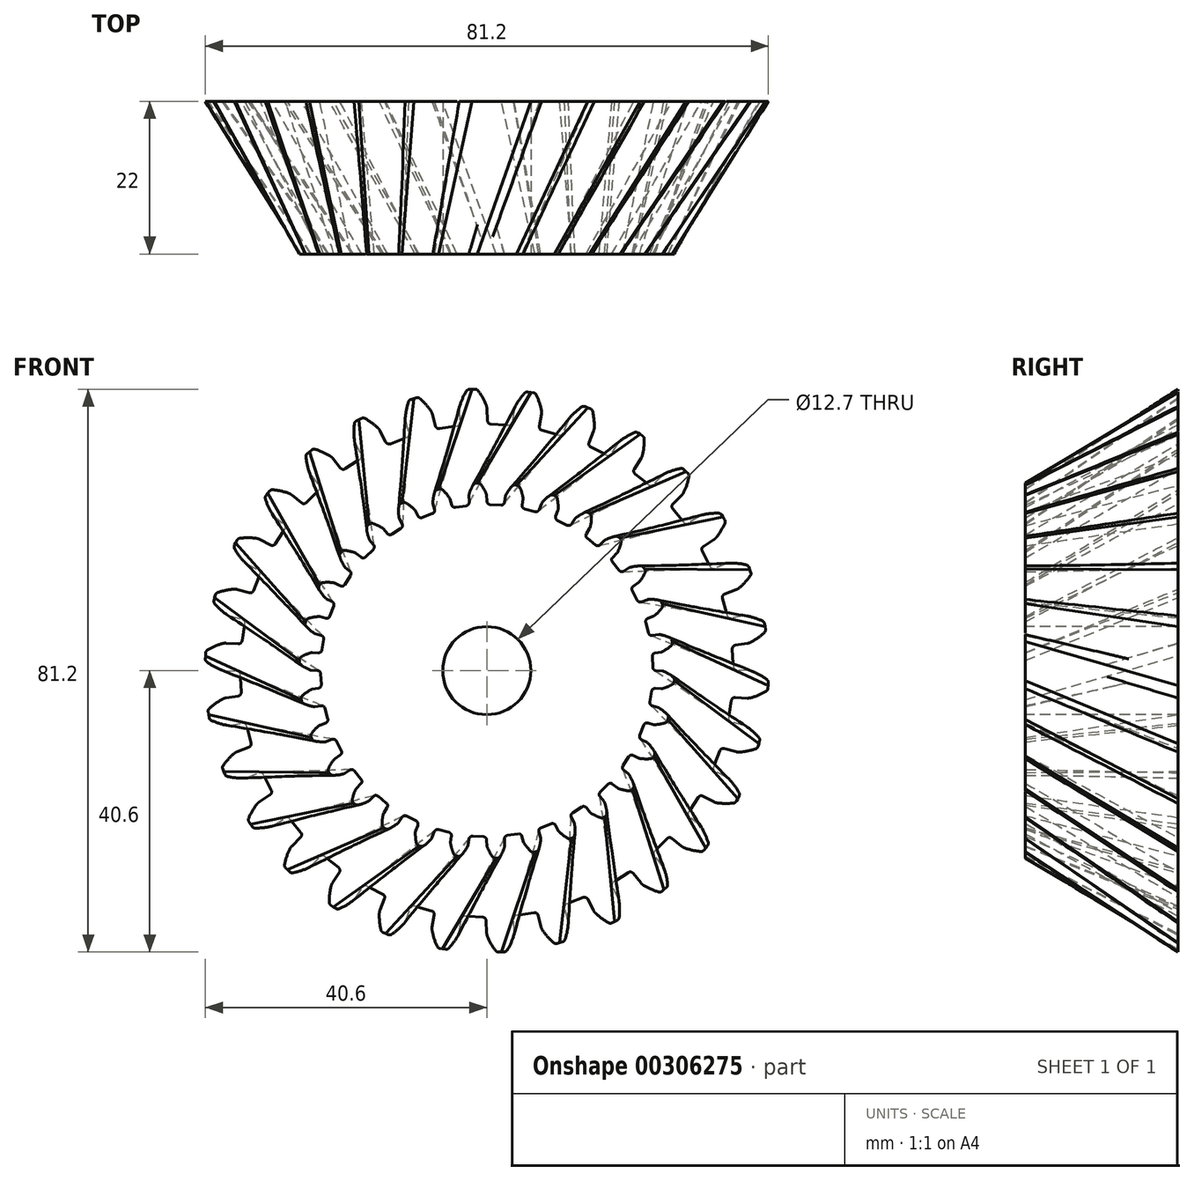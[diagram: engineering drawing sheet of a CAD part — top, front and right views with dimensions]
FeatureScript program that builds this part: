
annotation { "Feature Type Name" : "Feature", "Feature Type Description" : "" }
export const myFeature = defineFeature(function(context is Context, id is Id, definition is map)
    precondition{}
    {
        {
            var Q0;
            Q0=qCreatedBy(makeId("Front.planeOp"),FACE);
            var sketch = newSketch(context, id + "F0", { "sketchPlane" : qUnion([Q0])});
            skArc(sketch, "E0", {"start": v(-0.07, 25.48) * mm, "mid": v(-0.4, 26.19) * mm, "end": v(-0.83, 26.85) * mm});
            skLineSegment(sketch, "E1", {"start": v(-1.24, 27.06) * mm, "end": v(-1.82, 27.06) * mm});
            skLineSegment(sketch, "E2", {"start": v(-0.04, 25.32) * mm, "end": v(0, 24.44) * mm});
            skArc(sketch, "E3.MirrorCS", {"start": v(-2.56, 25.38) * mm, "mid": v(-2.3, 26.1) * mm, "end": v(-1.97, 26.78) * mm});
            skLineSegment(sketch, "E4.MirrorCS", {"start": v(-1.58, 27.03) * mm, "end": v(-0.9, 27.1) * mm});
            skLineSegment(sketch, "E5.MirrorCS", {"start": v(-2.58, 25.21) * mm, "end": v(-2.54, 24.3) * mm});
            skPoint(sketch, "E6.visualSharp", {"position": v(-2.5, 23.57) * mm});
            skArc(sketch, "E6.filletArc", {"start": v(-2.97, 23.78) * mm, "mid": v(-2.65, 23.96) * mm, "end": v(-2.54, 24.3) * mm});
            skPoint(sketch, "E7.visualSharp", {"position": v(0.05, 23.7) * mm});
            skArc(sketch, "E7.filletArc", {"start": v(0, 24.44) * mm, "mid": v(0.16, 24.1) * mm, "end": v(0.5, 23.96) * mm});
            skPoint(sketch, "E8.visualSharp", {"position": v(-2.59, 25.3) * mm});
            skArc(sketch, "E8.filletArc", {"start": v(-2.56, 25.38) * mm, "mid": v(-2.58, 25.3) * mm, "end": v(-2.58, 25.21) * mm});
            skPoint(sketch, "E9.visualSharp", {"position": v(-0.04, 25.4) * mm});
            skArc(sketch, "E9.filletArc", {"start": v(-0.04, 25.32) * mm, "mid": v(-0.05, 25.4) * mm, "end": v(-0.07, 25.48) * mm});
            skPoint(sketch, "E10.visualSharp", {"position": v(-0.99, 27.06) * mm});
            skArc(sketch, "E10.filletArc", {"start": v(-0.83, 26.85) * mm, "mid": v(-1, 27) * mm, "end": v(-1.24, 27.06) * mm});
            skPoint(sketch, "E11.visualSharp", {"position": v(-1.83, 27) * mm});
            skArc(sketch, "E11.filletArc", {"start": v(-1.58, 27.03) * mm, "mid": v(-1.8, 26.95) * mm, "end": v(-1.97, 26.78) * mm});
            skPoint(sketch, "E12.1.0", {"position": v(-6.6, 26.26) * mm});
            skLineSegment(sketch, "E12.1.1", {"start": v(-5.3, 24.75) * mm, "end": v(-5.07, 23.9) * mm});
            skArc(sketch, "E12.1.2", {"start": v(-5.07, 23.9) * mm, "mid": v(-4.85, 23.6) * mm, "end": v(-4.5, 23.54) * mm});
            skPoint(sketch, "E12.1.3", {"position": v(-4.88, 23.2) * mm});
            skArc(sketch, "E12.1.4", {"start": v(-7.78, 24.29) * mm, "mid": v(-7.69, 25.05) * mm, "end": v(-7.5, 25.78) * mm});
            skArc(sketch, "E12.1.5", {"start": v(-7.85, 22.64) * mm, "mid": v(-7.57, 22.88) * mm, "end": v(-7.53, 23.25) * mm});
            skLineSegment(sketch, "E12.1.6", {"start": v(-7.77, 24.12) * mm, "end": v(-7.53, 23.25) * mm});
            skArc(sketch, "E12.1.7", {"start": v(-5.37, 24.9) * mm, "mid": v(-5.84, 25.53) * mm, "end": v(-6.4, 26.09) * mm});
            skPoint(sketch, "E12.1.8", {"position": v(-7.34, 22.54) * mm});
            skPoint(sketch, "E12.1.9", {"position": v(-5.32, 24.83) * mm});
            skPoint(sketch, "E12.1.10", {"position": v(-7.79, 24.2) * mm});
            skPoint(sketch, "E12.1.11", {"position": v(-7.4, 26.03) * mm});
            skArc(sketch, "E12.1.12", {"start": v(-7.17, 26.11) * mm, "mid": v(-7.37, 25.99) * mm, "end": v(-7.5, 25.78) * mm});
            skArc(sketch, "E12.1.13", {"start": v(-6.4, 26.09) * mm, "mid": v(-6.6, 26.2) * mm, "end": v(-6.84, 26.2) * mm});
            skArc(sketch, "E12.1.14", {"start": v(-5.3, 24.75) * mm, "mid": v(-5.33, 24.83) * mm, "end": v(-5.37, 24.9) * mm});
            skArc(sketch, "E12.1.15", {"start": v(-7.78, 24.29) * mm, "mid": v(-7.78, 24.2) * mm, "end": v(-7.77, 24.12) * mm});
            skLineSegment(sketch, "E12.1.16", {"start": v(-6.84, 26.2) * mm, "end": v(-7.4, 26.09) * mm});
            skLineSegment(sketch, "E12.1.17", {"start": v(-7.17, 26.11) * mm, "end": v(-6.52, 26.32) * mm});
            skPoint(sketch, "E12.2.0", {"position": v(-11.9, 24.31) * mm});
            skLineSegment(sketch, "E12.2.1", {"start": v(-10.33, 23.11) * mm, "end": v(-9.93, 22.33) * mm});
            skArc(sketch, "E12.2.2", {"start": v(-9.93, 22.33) * mm, "mid": v(-9.66, 22.08) * mm, "end": v(-9.29, 22.09) * mm});
            skPoint(sketch, "E12.2.3", {"position": v(-9.6, 21.67) * mm});
            skArc(sketch, "E12.2.4", {"start": v(-12.66, 22.14) * mm, "mid": v(-12.72, 22.9) * mm, "end": v(-12.7, 23.66) * mm});
            skArc(sketch, "E12.2.5", {"start": v(-12.39, 20.51) * mm, "mid": v(-12.17, 20.8) * mm, "end": v(-12.2, 21.17) * mm});
            skLineSegment(sketch, "E12.2.6", {"start": v(-12.61, 21.98) * mm, "end": v(-12.2, 21.17) * mm});
            skArc(sketch, "E12.2.7", {"start": v(-10.43, 23.24) * mm, "mid": v(-11.02, 23.76) * mm, "end": v(-11.68, 24.19) * mm});
            skPoint(sketch, "E12.2.8", {"position": v(-11.87, 20.52) * mm});
            skPoint(sketch, "E12.2.9", {"position": v(-10.37, 23.18) * mm});
            skPoint(sketch, "E12.2.10", {"position": v(-12.65, 22.05) * mm});
            skPoint(sketch, "E12.2.11", {"position": v(-12.66, 23.92) * mm});
            skArc(sketch, "E12.2.12", {"start": v(-12.44, 24.05) * mm, "mid": v(-12.61, 23.89) * mm, "end": v(-12.7, 23.66) * mm});
            skArc(sketch, "E12.2.13", {"start": v(-11.68, 24.19) * mm, "mid": v(-11.9, 24.26) * mm, "end": v(-12.14, 24.21) * mm});
            skArc(sketch, "E12.2.14", {"start": v(-10.33, 23.11) * mm, "mid": v(-10.37, 23.18) * mm, "end": v(-10.43, 23.24) * mm});
            skArc(sketch, "E12.2.15", {"start": v(-12.66, 22.14) * mm, "mid": v(-12.65, 22.06) * mm, "end": v(-12.61, 21.98) * mm});
            skLineSegment(sketch, "E12.2.16", {"start": v(-12.14, 24.21) * mm, "end": v(-12.67, 23.98) * mm});
            skLineSegment(sketch, "E12.2.17", {"start": v(-12.44, 24.05) * mm, "end": v(-11.85, 24.4) * mm});
            skPoint(sketch, "E12.3.0", {"position": v(-16.7, 21.3) * mm});
            skLineSegment(sketch, "E12.3.1", {"start": v(-14.91, 20.46) * mm, "end": v(-14.36, 19.77) * mm});
            skArc(sketch, "E12.3.2", {"start": v(-14.36, 19.77) * mm, "mid": v(-14.04, 19.6) * mm, "end": v(-13.68, 19.67) * mm});
            skPoint(sketch, "E12.3.3", {"position": v(-13.9, 19.2) * mm});
            skArc(sketch, "E12.3.4", {"start": v(-17, 19.02) * mm, "mid": v(-17.2, 19.75) * mm, "end": v(-17.33, 20.5) * mm});
            skArc(sketch, "E12.3.5", {"start": v(-16.38, 17.49) * mm, "mid": v(-16.23, 17.82) * mm, "end": v(-16.34, 18.17) * mm});
            skLineSegment(sketch, "E12.3.6", {"start": v(-16.9, 18.88) * mm, "end": v(-16.34, 18.17) * mm});
            skArc(sketch, "E12.3.7", {"start": v(-15.03, 20.57) * mm, "mid": v(-15.72, 20.94) * mm, "end": v(-16.45, 21.23) * mm});
            skPoint(sketch, "E12.3.8", {"position": v(-15.88, 17.6) * mm});
            skPoint(sketch, "E12.3.9", {"position": v(-14.96, 20.52) * mm});
            skPoint(sketch, "E12.3.10", {"position": v(-16.96, 18.94) * mm});
            skPoint(sketch, "E12.3.11", {"position": v(-17.36, 20.77) * mm});
            skArc(sketch, "E12.3.12", {"start": v(-17.17, 20.94) * mm, "mid": v(-17.3, 20.74) * mm, "end": v(-17.33, 20.5) * mm});
            skArc(sketch, "E12.3.13", {"start": v(-16.45, 21.23) * mm, "mid": v(-16.69, 21.25) * mm, "end": v(-16.9, 21.16) * mm});
            skArc(sketch, "E12.3.14", {"start": v(-14.91, 20.46) * mm, "mid": v(-14.97, 20.52) * mm, "end": v(-15.03, 20.57) * mm});
            skArc(sketch, "E12.3.15", {"start": v(-17, 19.02) * mm, "mid": v(-16.96, 18.95) * mm, "end": v(-16.9, 18.88) * mm});
            skLineSegment(sketch, "E12.3.16", {"start": v(-16.9, 21.16) * mm, "end": v(-17.38, 20.82) * mm});
            skLineSegment(sketch, "E12.3.17", {"start": v(-17.17, 20.94) * mm, "end": v(-16.66, 21.4) * mm});
            skPoint(sketch, "E12.4.0", {"position": v(-20.77, 17.37) * mm});
            skLineSegment(sketch, "E12.4.1", {"start": v(-18.84, 16.91) * mm, "end": v(-18.15, 16.36) * mm});
            skArc(sketch, "E12.4.2", {"start": v(-18.15, 16.36) * mm, "mid": v(-17.8, 16.25) * mm, "end": v(-17.47, 16.4) * mm});
            skPoint(sketch, "E12.4.3", {"position": v(-17.58, 15.9) * mm});
            skArc(sketch, "E12.4.4", {"start": v(-20.57, 15.08) * mm, "mid": v(-20.94, 15.75) * mm, "end": v(-21.22, 16.45) * mm});
            skArc(sketch, "E12.4.5", {"start": v(-19.66, 13.7) * mm, "mid": v(-19.58, 14.06) * mm, "end": v(-19.76, 14.38) * mm});
            skLineSegment(sketch, "E12.4.6", {"start": v(-20.46, 14.95) * mm, "end": v(-19.76, 14.38) * mm});
            skArc(sketch, "E12.4.7", {"start": v(-18.98, 17) * mm, "mid": v(-19.73, 17.22) * mm, "end": v(-20.5, 17.35) * mm});
            skPoint(sketch, "E12.4.8", {"position": v(-19.2, 13.92) * mm});
            skPoint(sketch, "E12.4.9", {"position": v(-18.9, 16.96) * mm});
            skPoint(sketch, "E12.4.10", {"position": v(-20.53, 15) * mm});
            skPoint(sketch, "E12.4.11", {"position": v(-21.3, 16.7) * mm});
            skArc(sketch, "E12.4.12", {"start": v(-21.15, 16.91) * mm, "mid": v(-21.24, 16.7) * mm, "end": v(-21.22, 16.45) * mm});
            skArc(sketch, "E12.4.13", {"start": v(-20.5, 17.35) * mm, "mid": v(-20.74, 17.32) * mm, "end": v(-20.94, 17.18) * mm});
            skArc(sketch, "E12.4.14", {"start": v(-18.84, 16.91) * mm, "mid": v(-18.9, 16.96) * mm, "end": v(-18.98, 17) * mm});
            skArc(sketch, "E12.4.15", {"start": v(-20.57, 15.08) * mm, "mid": v(-20.52, 15) * mm, "end": v(-20.46, 14.95) * mm});
            skLineSegment(sketch, "E12.4.16", {"start": v(-20.94, 17.18) * mm, "end": v(-21.33, 16.75) * mm});
            skLineSegment(sketch, "E12.4.17", {"start": v(-21.15, 16.91) * mm, "end": v(-20.75, 17.46) * mm});
            skPoint(sketch, "E12.5.0", {"position": v(-23.93, 12.67) * mm});
            skLineSegment(sketch, "E12.5.1", {"start": v(-21.94, 12.62) * mm, "end": v(-21.16, 12.23) * mm});
            skArc(sketch, "E12.5.2", {"start": v(-21.16, 12.23) * mm, "mid": v(-20.8, 12.19) * mm, "end": v(-20.5, 12.4) * mm});
            skPoint(sketch, "E12.5.3", {"position": v(-20.5, 11.9) * mm});
            skArc(sketch, "E12.5.4", {"start": v(-23.26, 10.47) * mm, "mid": v(-23.75, 11.05) * mm, "end": v(-24.18, 11.68) * mm});
            skArc(sketch, "E12.5.5", {"start": v(-22.08, 9.31) * mm, "mid": v(-22.07, 9.68) * mm, "end": v(-22.32, 9.96) * mm});
            skLineSegment(sketch, "E12.5.6", {"start": v(-23.12, 10.37) * mm, "end": v(-22.32, 9.96) * mm});
            skArc(sketch, "E12.5.7", {"start": v(-22.1, 12.68) * mm, "mid": v(-22.88, 12.74) * mm, "end": v(-23.66, 12.7) * mm});
            skPoint(sketch, "E12.5.8", {"position": v(-21.67, 9.62) * mm});
            skPoint(sketch, "E12.5.9", {"position": v(-22.02, 12.66) * mm});
            skPoint(sketch, "E12.5.10", {"position": v(-23.2, 10.4) * mm});
            skPoint(sketch, "E12.5.11", {"position": v(-24.3, 11.91) * mm});
            skArc(sketch, "E12.5.12", {"start": v(-24.2, 12.14) * mm, "mid": v(-24.24, 11.91) * mm, "end": v(-24.18, 11.68) * mm});
            skArc(sketch, "E12.5.13", {"start": v(-23.66, 12.7) * mm, "mid": v(-23.89, 12.63) * mm, "end": v(-24.05, 12.45) * mm});
            skArc(sketch, "E12.5.14", {"start": v(-21.94, 12.62) * mm, "mid": v(-22.02, 12.66) * mm, "end": v(-22.1, 12.68) * mm});
            skArc(sketch, "E12.5.15", {"start": v(-23.26, 10.47) * mm, "mid": v(-23.2, 10.41) * mm, "end": v(-23.12, 10.37) * mm});
            skLineSegment(sketch, "E12.5.16", {"start": v(-24.05, 12.45) * mm, "end": v(-24.34, 11.95) * mm});
            skLineSegment(sketch, "E12.5.17", {"start": v(-24.2, 12.14) * mm, "end": v(-23.93, 12.77) * mm});
            skPoint(sketch, "E12.6.0", {"position": v(-26.04, 7.42) * mm});
            skLineSegment(sketch, "E12.6.1", {"start": v(-24.09, 7.79) * mm, "end": v(-23.24, 7.56) * mm});
            skArc(sketch, "E12.6.2", {"start": v(-23.24, 7.56) * mm, "mid": v(-22.87, 7.6) * mm, "end": v(-22.63, 7.88) * mm});
            skPoint(sketch, "E12.6.3", {"position": v(-22.53, 7.37) * mm});
            skArc(sketch, "E12.6.4", {"start": v(-24.93, 5.4) * mm, "mid": v(-25.53, 5.87) * mm, "end": v(-26.08, 6.4) * mm});
            skArc(sketch, "E12.6.5", {"start": v(-23.53, 4.52) * mm, "mid": v(-23.6, 4.88) * mm, "end": v(-23.9, 5.1) * mm});
            skLineSegment(sketch, "E12.6.6", {"start": v(-24.77, 5.33) * mm, "end": v(-23.9, 5.1) * mm});
            skArc(sketch, "E12.6.7", {"start": v(-24.25, 7.8) * mm, "mid": v(-25.03, 7.7) * mm, "end": v(-25.79, 7.5) * mm});
            skPoint(sketch, "E12.6.8", {"position": v(-23.2, 4.9) * mm});
            skPoint(sketch, "E12.6.9", {"position": v(-24.17, 7.8) * mm});
            skPoint(sketch, "E12.6.10", {"position": v(-24.86, 5.36) * mm});
            skPoint(sketch, "E12.6.11", {"position": v(-26.25, 6.6) * mm});
            skArc(sketch, "E12.6.12", {"start": v(-26.2, 6.85) * mm, "mid": v(-26.2, 6.6) * mm, "end": v(-26.08, 6.4) * mm});
            skArc(sketch, "E12.6.13", {"start": v(-25.79, 7.5) * mm, "mid": v(-26, 7.38) * mm, "end": v(-26.11, 7.18) * mm});
            skArc(sketch, "E12.6.14", {"start": v(-24.09, 7.79) * mm, "mid": v(-24.17, 7.8) * mm, "end": v(-24.25, 7.8) * mm});
            skArc(sketch, "E12.6.15", {"start": v(-24.93, 5.4) * mm, "mid": v(-24.85, 5.36) * mm, "end": v(-24.77, 5.33) * mm});
            skLineSegment(sketch, "E12.6.16", {"start": v(-26.11, 7.18) * mm, "end": v(-26.3, 6.63) * mm});
            skLineSegment(sketch, "E12.6.17", {"start": v(-26.2, 6.85) * mm, "end": v(-26.06, 7.51) * mm});
            skPoint(sketch, "E12.7.0", {"position": v(-27.01, 1.85) * mm});
            skLineSegment(sketch, "E12.7.1", {"start": v(-25.18, 2.6) * mm, "end": v(-24.3, 2.56) * mm});
            skArc(sketch, "E12.7.2", {"start": v(-24.3, 2.56) * mm, "mid": v(-23.95, 2.68) * mm, "end": v(-23.77, 3) * mm});
            skPoint(sketch, "E12.7.3", {"position": v(-23.57, 2.52) * mm});
            skArc(sketch, "E12.7.4", {"start": v(-25.5, 0.1) * mm, "mid": v(-26.2, 0.43) * mm, "end": v(-26.84, 0.84) * mm});
            skArc(sketch, "E12.7.5", {"start": v(-23.96, -0.47) * mm, "mid": v(-24.1, -0.13) * mm, "end": v(-24.44, 0.02) * mm});
            skLineSegment(sketch, "E12.7.6", {"start": v(-25.34, 0.07) * mm, "end": v(-24.44, 0.02) * mm});
            skArc(sketch, "E12.7.7", {"start": v(-25.35, 2.6) * mm, "mid": v(-26.08, 2.33) * mm, "end": v(-26.79, 1.98) * mm});
            skPoint(sketch, "E12.7.8", {"position": v(-23.7, -0.02) * mm});
            skPoint(sketch, "E12.7.9", {"position": v(-25.26, 2.61) * mm});
            skPoint(sketch, "E12.7.10", {"position": v(-25.43, 0.07) * mm});
            skPoint(sketch, "E12.7.11", {"position": v(-27.05, 1) * mm});
            skArc(sketch, "E12.7.12", {"start": v(-27.05, 1.25) * mm, "mid": v(-27, 1.02) * mm, "end": v(-26.84, 0.84) * mm});
            skArc(sketch, "E12.7.13", {"start": v(-26.79, 1.98) * mm, "mid": v(-26.96, 1.82) * mm, "end": v(-27.04, 1.6) * mm});
            skArc(sketch, "E12.7.14", {"start": v(-25.18, 2.6) * mm, "mid": v(-25.26, 2.6) * mm, "end": v(-25.35, 2.6) * mm});
            skArc(sketch, "E12.7.15", {"start": v(-25.5, 0.1) * mm, "mid": v(-25.43, 0.08) * mm, "end": v(-25.34, 0.07) * mm});
            skLineSegment(sketch, "E12.7.16", {"start": v(-27.04, 1.6) * mm, "end": v(-27.1, 1.02) * mm});
            skLineSegment(sketch, "E12.7.17", {"start": v(-27.05, 1.25) * mm, "end": v(-27.05, 1.93) * mm});
            skPoint(sketch, "E12.8.0", {"position": v(-26.8, -3.81) * mm});
            skLineSegment(sketch, "E12.8.1", {"start": v(-25.17, -2.68) * mm, "end": v(-24.3, -2.55) * mm});
            skArc(sketch, "E12.8.2", {"start": v(-24.3, -2.55) * mm, "mid": v(-23.99, -2.36) * mm, "end": v(-23.88, -2) * mm});
            skPoint(sketch, "E12.8.3", {"position": v(-23.58, -2.43) * mm});
            skArc(sketch, "E12.8.4", {"start": v(-24.97, -5.2) * mm, "mid": v(-25.71, -5.03) * mm, "end": v(-26.43, -4.76) * mm});
            skArc(sketch, "E12.8.5", {"start": v(-23.34, -5.44) * mm, "mid": v(-23.55, -5.14) * mm, "end": v(-23.9, -5.06) * mm});
            skLineSegment(sketch, "E12.8.6", {"start": v(-24.8, -5.2) * mm, "end": v(-23.9, -5.06) * mm});
            skArc(sketch, "E12.8.7", {"start": v(-25.33, -2.74) * mm, "mid": v(-26, -3.14) * mm, "end": v(-26.61, -3.63) * mm});
            skPoint(sketch, "E12.8.8", {"position": v(-23.18, -4.95) * mm});
            skPoint(sketch, "E12.8.9", {"position": v(-25.25, -2.7) * mm});
            skPoint(sketch, "E12.8.10", {"position": v(-24.88, -5.22) * mm});
            skPoint(sketch, "E12.8.11", {"position": v(-26.67, -4.65) * mm});
            skArc(sketch, "E12.8.12", {"start": v(-26.72, -4.4) * mm, "mid": v(-26.62, -4.61) * mm, "end": v(-26.43, -4.76) * mm});
            skArc(sketch, "E12.8.13", {"start": v(-26.61, -3.63) * mm, "mid": v(-26.75, -3.83) * mm, "end": v(-26.78, -4.06) * mm});
            skArc(sketch, "E12.8.14", {"start": v(-25.17, -2.68) * mm, "mid": v(-25.25, -2.7) * mm, "end": v(-25.33, -2.74) * mm});
            skArc(sketch, "E12.8.15", {"start": v(-24.97, -5.2) * mm, "mid": v(-24.89, -5.21) * mm, "end": v(-24.8, -5.2) * mm});
            skLineSegment(sketch, "E12.8.16", {"start": v(-26.78, -4.06) * mm, "end": v(-26.72, -4.64) * mm});
            skLineSegment(sketch, "E12.8.17", {"start": v(-26.72, -4.4) * mm, "end": v(-26.86, -3.74) * mm});
            skPoint(sketch, "E12.9.0", {"position": v(-25.43, -9.3) * mm});
            skLineSegment(sketch, "E12.9.1", {"start": v(-24.06, -7.86) * mm, "end": v(-23.24, -7.54) * mm});
            skArc(sketch, "E12.9.2", {"start": v(-23.24, -7.54) * mm, "mid": v(-22.97, -7.3) * mm, "end": v(-22.94, -6.93) * mm});
            skPoint(sketch, "E12.9.3", {"position": v(-22.56, -7.28) * mm});
            skArc(sketch, "E12.9.4", {"start": v(-23.34, -10.28) * mm, "mid": v(-24.1, -10.26) * mm, "end": v(-24.86, -10.15) * mm});
            skArc(sketch, "E12.9.5", {"start": v(-21.7, -10.17) * mm, "mid": v(-21.97, -9.92) * mm, "end": v(-22.33, -9.92) * mm});
            skLineSegment(sketch, "E12.9.6", {"start": v(-23.18, -10.25) * mm, "end": v(-22.33, -9.92) * mm});
            skArc(sketch, "E12.9.7", {"start": v(-24.2, -7.94) * mm, "mid": v(-24.78, -8.48) * mm, "end": v(-25.28, -9.08) * mm});
            skPoint(sketch, "E12.9.8", {"position": v(-21.65, -9.66) * mm});
            skPoint(sketch, "E12.9.9", {"position": v(-24.14, -7.89) * mm});
            skPoint(sketch, "E12.9.10", {"position": v(-23.26, -10.28) * mm});
            skPoint(sketch, "E12.9.11", {"position": v(-25.12, -10.1) * mm});
            skArc(sketch, "E12.9.12", {"start": v(-25.22, -9.86) * mm, "mid": v(-25.07, -10.05) * mm, "end": v(-24.86, -10.15) * mm});
            skArc(sketch, "E12.9.13", {"start": v(-25.28, -9.08) * mm, "mid": v(-25.37, -9.3) * mm, "end": v(-25.35, -9.54) * mm});
            skArc(sketch, "E12.9.14", {"start": v(-24.06, -7.86) * mm, "mid": v(-24.14, -7.9) * mm, "end": v(-24.2, -7.94) * mm});
            skArc(sketch, "E12.9.15", {"start": v(-23.34, -10.28) * mm, "mid": v(-23.26, -10.27) * mm, "end": v(-23.18, -10.25) * mm});
            skLineSegment(sketch, "E12.9.16", {"start": v(-25.35, -9.54) * mm, "end": v(-25.17, -10.1) * mm});
            skLineSegment(sketch, "E12.9.17", {"start": v(-25.22, -9.86) * mm, "end": v(-25.5, -9.24) * mm});
            skPoint(sketch, "E12.10.0", {"position": v(-22.94, -14.38) * mm});
            skLineSegment(sketch, "E12.10.1", {"start": v(-21.9, -12.7) * mm, "end": v(-21.17, -12.21) * mm});
            skArc(sketch, "E12.10.2", {"start": v(-21.17, -12.21) * mm, "mid": v(-20.95, -11.91) * mm, "end": v(-21, -11.55) * mm});
            skPoint(sketch, "E12.10.3", {"position": v(-20.55, -11.81) * mm});
            skArc(sketch, "E12.10.4", {"start": v(-20.7, -14.9) * mm, "mid": v(-21.45, -15.05) * mm, "end": v(-22.2, -15.1) * mm});
            skArc(sketch, "E12.10.5", {"start": v(-19.1, -14.46) * mm, "mid": v(-19.42, -14.27) * mm, "end": v(-19.78, -14.35) * mm});
            skLineSegment(sketch, "E12.10.6", {"start": v(-20.54, -14.84) * mm, "end": v(-19.78, -14.35) * mm});
            skArc(sketch, "E12.10.7", {"start": v(-22.03, -12.8) * mm, "mid": v(-22.47, -13.45) * mm, "end": v(-22.83, -14.14) * mm});
            skPoint(sketch, "E12.10.8", {"position": v(-19.17, -13.95) * mm});
            skPoint(sketch, "E12.10.9", {"position": v(-21.97, -12.74) * mm});
            skPoint(sketch, "E12.10.10", {"position": v(-20.61, -14.89) * mm});
            skPoint(sketch, "E12.10.11", {"position": v(-22.47, -15.1) * mm});
            skArc(sketch, "E12.10.12", {"start": v(-22.62, -14.89) * mm, "mid": v(-22.44, -15.04) * mm, "end": v(-22.2, -15.1) * mm});
            skArc(sketch, "E12.10.13", {"start": v(-22.83, -14.14) * mm, "mid": v(-22.88, -14.37) * mm, "end": v(-22.81, -14.6) * mm});
            skArc(sketch, "E12.10.14", {"start": v(-21.9, -12.7) * mm, "mid": v(-21.97, -12.74) * mm, "end": v(-22.03, -12.8) * mm});
            skArc(sketch, "E12.10.15", {"start": v(-20.7, -14.9) * mm, "mid": v(-20.62, -14.88) * mm, "end": v(-20.54, -14.84) * mm});
            skLineSegment(sketch, "E12.10.16", {"start": v(-22.81, -14.6) * mm, "end": v(-22.52, -15.1) * mm});
            skLineSegment(sketch, "E12.10.17", {"start": v(-22.62, -14.89) * mm, "end": v(-23.02, -14.34) * mm});
            skPoint(sketch, "E12.11.0", {"position": v(-19.44, -18.84) * mm});
            skLineSegment(sketch, "E12.11.1", {"start": v(-18.79, -16.97) * mm, "end": v(-18.17, -16.34) * mm});
            skArc(sketch, "E12.11.2", {"start": v(-18.17, -16.34) * mm, "mid": v(-18.02, -16) * mm, "end": v(-18.14, -15.66) * mm});
            skPoint(sketch, "E12.11.3", {"position": v(-17.65, -15.83) * mm});
            skArc(sketch, "E12.11.4", {"start": v(-17.14, -18.89) * mm, "mid": v(-17.85, -19.18) * mm, "end": v(-18.58, -19.38) * mm});
            skArc(sketch, "E12.11.5", {"start": v(-15.68, -18.12) * mm, "mid": v(-16.03, -18) * mm, "end": v(-16.37, -18.15) * mm});
            skLineSegment(sketch, "E12.11.6", {"start": v(-17, -18.79) * mm, "end": v(-16.37, -18.15) * mm});
            skArc(sketch, "E12.11.7", {"start": v(-18.88, -17.1) * mm, "mid": v(-19.19, -17.83) * mm, "end": v(-19.4, -18.58) * mm});
            skPoint(sketch, "E12.11.8", {"position": v(-15.85, -17.63) * mm});
            skPoint(sketch, "E12.11.9", {"position": v(-18.85, -17.03) * mm});
            skPoint(sketch, "E12.11.10", {"position": v(-17.07, -18.85) * mm});
            skPoint(sketch, "E12.11.11", {"position": v(-18.84, -19.43) * mm});
            skArc(sketch, "E12.11.12", {"start": v(-19.03, -19.26) * mm, "mid": v(-18.82, -19.38) * mm, "end": v(-18.58, -19.38) * mm});
            skArc(sketch, "E12.11.13", {"start": v(-19.4, -18.58) * mm, "mid": v(-19.39, -18.82) * mm, "end": v(-19.28, -19.03) * mm});
            skArc(sketch, "E12.11.14", {"start": v(-18.79, -16.97) * mm, "mid": v(-18.84, -17.03) * mm, "end": v(-18.88, -17.1) * mm});
            skArc(sketch, "E12.11.15", {"start": v(-17.14, -18.89) * mm, "mid": v(-17.07, -18.84) * mm, "end": v(-17, -18.79) * mm});
            skLineSegment(sketch, "E12.11.16", {"start": v(-19.28, -19.03) * mm, "end": v(-18.89, -19.46) * mm});
            skLineSegment(sketch, "E12.11.17", {"start": v(-19.03, -19.26) * mm, "end": v(-19.53, -18.8) * mm});
            skPoint(sketch, "E12.12.0", {"position": v(-15.1, -22.47) * mm});
            skLineSegment(sketch, "E12.12.1", {"start": v(-14.85, -20.5) * mm, "end": v(-14.37, -19.76) * mm});
            skArc(sketch, "E12.12.2", {"start": v(-14.37, -19.76) * mm, "mid": v(-14.3, -19.4) * mm, "end": v(-14.48, -19.09) * mm});
            skPoint(sketch, "E12.12.3", {"position": v(-13.97, -19.15) * mm});
            skArc(sketch, "E12.12.4", {"start": v(-12.84, -22.04) * mm, "mid": v(-13.47, -22.47) * mm, "end": v(-14.15, -22.82) * mm});
            skArc(sketch, "E12.12.5", {"start": v(-11.57, -20.98) * mm, "mid": v(-11.94, -20.94) * mm, "end": v(-12.24, -21.16) * mm});
            skLineSegment(sketch, "E12.12.6", {"start": v(-12.73, -21.91) * mm, "end": v(-12.24, -21.16) * mm});
            skArc(sketch, "E12.12.7", {"start": v(-14.92, -20.65) * mm, "mid": v(-15.06, -21.42) * mm, "end": v(-15.1, -22.2) * mm});
            skPoint(sketch, "E12.12.8", {"position": v(-11.84, -20.54) * mm});
            skPoint(sketch, "E12.12.9", {"position": v(-14.9, -20.57) * mm});
            skPoint(sketch, "E12.12.10", {"position": v(-12.77, -21.98) * mm});
            skPoint(sketch, "E12.12.11", {"position": v(-14.39, -22.93) * mm});
            skArc(sketch, "E12.12.12", {"start": v(-14.6, -22.8) * mm, "mid": v(-14.38, -22.87) * mm, "end": v(-14.15, -22.82) * mm});
            skArc(sketch, "E12.12.13", {"start": v(-15.1, -22.2) * mm, "mid": v(-15.05, -22.44) * mm, "end": v(-14.9, -22.62) * mm});
            skArc(sketch, "E12.12.14", {"start": v(-14.85, -20.5) * mm, "mid": v(-14.89, -20.58) * mm, "end": v(-14.92, -20.65) * mm});
            skArc(sketch, "E12.12.15", {"start": v(-12.84, -22.04) * mm, "mid": v(-12.78, -21.98) * mm, "end": v(-12.73, -21.91) * mm});
            skLineSegment(sketch, "E12.12.16", {"start": v(-14.9, -22.62) * mm, "end": v(-14.43, -22.96) * mm});
            skLineSegment(sketch, "E12.12.17", {"start": v(-14.6, -22.8) * mm, "end": v(-15.2, -22.46) * mm});
            skPoint(sketch, "E12.13.0", {"position": v(-10.1, -25.12) * mm});
            skLineSegment(sketch, "E12.13.1", {"start": v(-10.26, -23.14) * mm, "end": v(-9.95, -22.32) * mm});
            skArc(sketch, "E12.13.2", {"start": v(-9.95, -22.32) * mm, "mid": v(-9.95, -21.95) * mm, "end": v(-10.2, -21.68) * mm});
            skPoint(sketch, "E12.13.3", {"position": v(-9.68, -21.64) * mm});
            skArc(sketch, "E12.13.4", {"start": v(-7.98, -24.23) * mm, "mid": v(-8.5, -24.78) * mm, "end": v(-9.1, -25.27) * mm});
            skArc(sketch, "E12.13.5", {"start": v(-6.96, -22.93) * mm, "mid": v(-7.32, -22.96) * mm, "end": v(-7.57, -23.24) * mm});
            skLineSegment(sketch, "E12.13.6", {"start": v(-7.9, -24.08) * mm, "end": v(-7.57, -23.24) * mm});
            skArc(sketch, "E12.13.7", {"start": v(-10.3, -23.3) * mm, "mid": v(-10.28, -24.09) * mm, "end": v(-10.16, -24.86) * mm});
            skPoint(sketch, "E12.13.8", {"position": v(-7.3, -22.55) * mm});
            skPoint(sketch, "E12.13.9", {"position": v(-10.3, -23.22) * mm});
            skPoint(sketch, "E12.13.10", {"position": v(-7.92, -24.16) * mm});
            skPoint(sketch, "E12.13.11", {"position": v(-9.3, -25.42) * mm});
            skArc(sketch, "E12.13.12", {"start": v(-9.55, -25.34) * mm, "mid": v(-9.31, -25.36) * mm, "end": v(-9.1, -25.27) * mm});
            skArc(sketch, "E12.13.13", {"start": v(-10.16, -24.86) * mm, "mid": v(-10.06, -25.08) * mm, "end": v(-9.87, -25.22) * mm});
            skArc(sketch, "E12.13.14", {"start": v(-10.26, -23.14) * mm, "mid": v(-10.29, -23.22) * mm, "end": v(-10.3, -23.3) * mm});
            skArc(sketch, "E12.13.15", {"start": v(-7.98, -24.23) * mm, "mid": v(-7.93, -24.16) * mm, "end": v(-7.9, -24.08) * mm});
            skLineSegment(sketch, "E12.13.16", {"start": v(-9.87, -25.22) * mm, "end": v(-9.34, -25.46) * mm});
            skLineSegment(sketch, "E12.13.17", {"start": v(-9.55, -25.34) * mm, "end": v(-10.2, -25.13) * mm});
            skPoint(sketch, "E12.14.0", {"position": v(-4.66, -26.67) * mm});
            skLineSegment(sketch, "E12.14.1", {"start": v(-5.23, -24.77) * mm, "end": v(-5.09, -23.9) * mm});
            skArc(sketch, "E12.14.2", {"start": v(-5.09, -23.9) * mm, "mid": v(-5.17, -23.54) * mm, "end": v(-5.47, -23.33) * mm});
            skPoint(sketch, "E12.14.3", {"position": v(-4.97, -23.18) * mm});
            skArc(sketch, "E12.14.4", {"start": v(-2.77, -25.36) * mm, "mid": v(-3.17, -26) * mm, "end": v(-3.64, -26.6) * mm});
            skArc(sketch, "E12.14.5", {"start": v(-2.04, -23.88) * mm, "mid": v(-2.39, -23.98) * mm, "end": v(-2.57, -24.3) * mm});
            skLineSegment(sketch, "E12.14.6", {"start": v(-2.71, -25.2) * mm, "end": v(-2.57, -24.3) * mm});
            skArc(sketch, "E12.14.7", {"start": v(-5.23, -24.94) * mm, "mid": v(-5.04, -25.7) * mm, "end": v(-4.77, -26.43) * mm});
            skPoint(sketch, "E12.14.8", {"position": v(-2.46, -23.58) * mm});
            skPoint(sketch, "E12.14.9", {"position": v(-5.24, -24.85) * mm});
            skPoint(sketch, "E12.14.10", {"position": v(-2.73, -25.28) * mm});
            skPoint(sketch, "E12.14.11", {"position": v(-3.82, -26.8) * mm});
            skArc(sketch, "E12.14.12", {"start": v(-4.07, -26.77) * mm, "mid": v(-3.84, -26.74) * mm, "end": v(-3.64, -26.6) * mm});
            skArc(sketch, "E12.14.13", {"start": v(-4.77, -26.43) * mm, "mid": v(-4.63, -26.62) * mm, "end": v(-4.41, -26.72) * mm});
            skArc(sketch, "E12.14.14", {"start": v(-5.23, -24.77) * mm, "mid": v(-5.23, -24.85) * mm, "end": v(-5.23, -24.94) * mm});
            skArc(sketch, "E12.14.15", {"start": v(-2.77, -25.36) * mm, "mid": v(-2.73, -25.28) * mm, "end": v(-2.71, -25.2) * mm});
            skLineSegment(sketch, "E12.14.16", {"start": v(-4.41, -26.72) * mm, "end": v(-3.84, -26.84) * mm});
            skLineSegment(sketch, "E12.14.17", {"start": v(-4.07, -26.77) * mm, "end": v(-4.75, -26.7) * mm});
            skPoint(sketch, "E12.15.0", {"position": v(0.99, -27.06) * mm});
            skLineSegment(sketch, "E12.15.1", {"start": v(0.04, -25.32) * mm, "end": v(0, -24.44) * mm});
            skArc(sketch, "E12.15.2", {"start": v(0, -24.44) * mm, "mid": v(-0.16, -24.1) * mm, "end": v(-0.5, -23.96) * mm});
            skPoint(sketch, "E12.15.3", {"position": v(-0.05, -23.7) * mm});
            skArc(sketch, "E12.15.4", {"start": v(2.56, -25.38) * mm, "mid": v(2.3, -26.1) * mm, "end": v(1.97, -26.78) * mm});
            skArc(sketch, "E12.15.5", {"start": v(2.97, -23.78) * mm, "mid": v(2.65, -23.96) * mm, "end": v(2.54, -24.3) * mm});
            skLineSegment(sketch, "E12.15.6", {"start": v(2.58, -25.21) * mm, "end": v(2.54, -24.3) * mm});
            skArc(sketch, "E12.15.7", {"start": v(0.07, -25.48) * mm, "mid": v(0.4, -26.19) * mm, "end": v(0.83, -26.85) * mm});
            skPoint(sketch, "E12.15.8", {"position": v(2.5, -23.57) * mm});
            skPoint(sketch, "E12.15.9", {"position": v(0.04, -25.4) * mm});
            skPoint(sketch, "E12.15.10", {"position": v(2.59, -25.3) * mm});
            skPoint(sketch, "E12.15.11", {"position": v(1.83, -27) * mm});
            skArc(sketch, "E12.15.12", {"start": v(1.58, -27.03) * mm, "mid": v(1.8, -26.95) * mm, "end": v(1.97, -26.78) * mm});
            skArc(sketch, "E12.15.13", {"start": v(0.83, -26.85) * mm, "mid": v(1, -27) * mm, "end": v(1.24, -27.06) * mm});
            skArc(sketch, "E12.15.14", {"start": v(0.04, -25.32) * mm, "mid": v(0.05, -25.4) * mm, "end": v(0.07, -25.48) * mm});
            skArc(sketch, "E12.15.15", {"start": v(2.56, -25.38) * mm, "mid": v(2.58, -25.3) * mm, "end": v(2.58, -25.21) * mm});
            skLineSegment(sketch, "E12.15.16", {"start": v(1.24, -27.06) * mm, "end": v(1.82, -27.06) * mm});
            skLineSegment(sketch, "E12.15.17", {"start": v(1.58, -27.03) * mm, "end": v(0.9, -27.1) * mm});
            skPoint(sketch, "E12.16.0", {"position": v(6.6, -26.26) * mm});
            skLineSegment(sketch, "E12.16.1", {"start": v(5.3, -24.75) * mm, "end": v(5.07, -23.9) * mm});
            skArc(sketch, "E12.16.2", {"start": v(5.07, -23.9) * mm, "mid": v(4.85, -23.6) * mm, "end": v(4.5, -23.54) * mm});
            skPoint(sketch, "E12.16.3", {"position": v(4.88, -23.2) * mm});
            skArc(sketch, "E12.16.4", {"start": v(7.78, -24.29) * mm, "mid": v(7.69, -25.05) * mm, "end": v(7.5, -25.78) * mm});
            skArc(sketch, "E12.16.5", {"start": v(7.85, -22.64) * mm, "mid": v(7.57, -22.88) * mm, "end": v(7.53, -23.25) * mm});
            skLineSegment(sketch, "E12.16.6", {"start": v(7.77, -24.12) * mm, "end": v(7.53, -23.25) * mm});
            skArc(sketch, "E12.16.7", {"start": v(5.37, -24.9) * mm, "mid": v(5.84, -25.53) * mm, "end": v(6.4, -26.09) * mm});
            skPoint(sketch, "E12.16.8", {"position": v(7.34, -22.54) * mm});
            skPoint(sketch, "E12.16.9", {"position": v(5.32, -24.83) * mm});
            skPoint(sketch, "E12.16.10", {"position": v(7.79, -24.2) * mm});
            skPoint(sketch, "E12.16.11", {"position": v(7.4, -26.03) * mm});
            skArc(sketch, "E12.16.12", {"start": v(7.17, -26.11) * mm, "mid": v(7.37, -25.99) * mm, "end": v(7.5, -25.78) * mm});
            skArc(sketch, "E12.16.13", {"start": v(6.4, -26.09) * mm, "mid": v(6.6, -26.2) * mm, "end": v(6.84, -26.2) * mm});
            skArc(sketch, "E12.16.14", {"start": v(5.3, -24.75) * mm, "mid": v(5.33, -24.83) * mm, "end": v(5.37, -24.9) * mm});
            skArc(sketch, "E12.16.15", {"start": v(7.78, -24.29) * mm, "mid": v(7.78, -24.2) * mm, "end": v(7.77, -24.12) * mm});
            skLineSegment(sketch, "E12.16.16", {"start": v(6.84, -26.2) * mm, "end": v(7.4, -26.09) * mm});
            skLineSegment(sketch, "E12.16.17", {"start": v(7.17, -26.11) * mm, "end": v(6.52, -26.32) * mm});
            skPoint(sketch, "E12.17.0", {"position": v(11.9, -24.31) * mm});
            skLineSegment(sketch, "E12.17.1", {"start": v(10.33, -23.11) * mm, "end": v(9.93, -22.33) * mm});
            skArc(sketch, "E12.17.2", {"start": v(9.93, -22.33) * mm, "mid": v(9.66, -22.08) * mm, "end": v(9.29, -22.09) * mm});
            skPoint(sketch, "E12.17.3", {"position": v(9.6, -21.67) * mm});
            skArc(sketch, "E12.17.4", {"start": v(12.66, -22.14) * mm, "mid": v(12.72, -22.9) * mm, "end": v(12.7, -23.66) * mm});
            skArc(sketch, "E12.17.5", {"start": v(12.39, -20.51) * mm, "mid": v(12.17, -20.8) * mm, "end": v(12.2, -21.17) * mm});
            skLineSegment(sketch, "E12.17.6", {"start": v(12.61, -21.98) * mm, "end": v(12.2, -21.17) * mm});
            skArc(sketch, "E12.17.7", {"start": v(10.43, -23.24) * mm, "mid": v(11.02, -23.76) * mm, "end": v(11.68, -24.19) * mm});
            skPoint(sketch, "E12.17.8", {"position": v(11.87, -20.52) * mm});
            skPoint(sketch, "E12.17.9", {"position": v(10.37, -23.18) * mm});
            skPoint(sketch, "E12.17.10", {"position": v(12.65, -22.05) * mm});
            skPoint(sketch, "E12.17.11", {"position": v(12.66, -23.92) * mm});
            skArc(sketch, "E12.17.12", {"start": v(12.44, -24.05) * mm, "mid": v(12.61, -23.89) * mm, "end": v(12.7, -23.66) * mm});
            skArc(sketch, "E12.17.13", {"start": v(11.68, -24.19) * mm, "mid": v(11.9, -24.26) * mm, "end": v(12.14, -24.21) * mm});
            skArc(sketch, "E12.17.14", {"start": v(10.33, -23.11) * mm, "mid": v(10.37, -23.18) * mm, "end": v(10.43, -23.24) * mm});
            skArc(sketch, "E12.17.15", {"start": v(12.66, -22.14) * mm, "mid": v(12.65, -22.06) * mm, "end": v(12.61, -21.98) * mm});
            skLineSegment(sketch, "E12.17.16", {"start": v(12.14, -24.21) * mm, "end": v(12.67, -23.98) * mm});
            skLineSegment(sketch, "E12.17.17", {"start": v(12.44, -24.05) * mm, "end": v(11.85, -24.4) * mm});
            skPoint(sketch, "E12.18.0", {"position": v(16.7, -21.3) * mm});
            skLineSegment(sketch, "E12.18.1", {"start": v(14.91, -20.46) * mm, "end": v(14.36, -19.77) * mm});
            skArc(sketch, "E12.18.2", {"start": v(14.36, -19.77) * mm, "mid": v(14.04, -19.6) * mm, "end": v(13.68, -19.67) * mm});
            skPoint(sketch, "E12.18.3", {"position": v(13.9, -19.2) * mm});
            skArc(sketch, "E12.18.4", {"start": v(17, -19.02) * mm, "mid": v(17.2, -19.75) * mm, "end": v(17.33, -20.5) * mm});
            skArc(sketch, "E12.18.5", {"start": v(16.38, -17.49) * mm, "mid": v(16.23, -17.82) * mm, "end": v(16.34, -18.17) * mm});
            skLineSegment(sketch, "E12.18.6", {"start": v(16.9, -18.88) * mm, "end": v(16.34, -18.17) * mm});
            skArc(sketch, "E12.18.7", {"start": v(15.03, -20.57) * mm, "mid": v(15.72, -20.94) * mm, "end": v(16.45, -21.23) * mm});
            skPoint(sketch, "E12.18.8", {"position": v(15.88, -17.6) * mm});
            skPoint(sketch, "E12.18.9", {"position": v(14.96, -20.52) * mm});
            skPoint(sketch, "E12.18.10", {"position": v(16.96, -18.94) * mm});
            skPoint(sketch, "E12.18.11", {"position": v(17.36, -20.77) * mm});
            skArc(sketch, "E12.18.12", {"start": v(17.17, -20.94) * mm, "mid": v(17.3, -20.74) * mm, "end": v(17.33, -20.5) * mm});
            skArc(sketch, "E12.18.13", {"start": v(16.45, -21.23) * mm, "mid": v(16.69, -21.25) * mm, "end": v(16.9, -21.16) * mm});
            skArc(sketch, "E12.18.14", {"start": v(14.91, -20.46) * mm, "mid": v(14.97, -20.52) * mm, "end": v(15.03, -20.57) * mm});
            skArc(sketch, "E12.18.15", {"start": v(17, -19.02) * mm, "mid": v(16.96, -18.95) * mm, "end": v(16.9, -18.88) * mm});
            skLineSegment(sketch, "E12.18.16", {"start": v(16.9, -21.16) * mm, "end": v(17.38, -20.82) * mm});
            skLineSegment(sketch, "E12.18.17", {"start": v(17.17, -20.94) * mm, "end": v(16.66, -21.4) * mm});
            skPoint(sketch, "E12.19.0", {"position": v(20.77, -17.37) * mm});
            skLineSegment(sketch, "E12.19.1", {"start": v(18.84, -16.91) * mm, "end": v(18.15, -16.36) * mm});
            skArc(sketch, "E12.19.2", {"start": v(18.15, -16.36) * mm, "mid": v(17.8, -16.25) * mm, "end": v(17.47, -16.4) * mm});
            skPoint(sketch, "E12.19.3", {"position": v(17.58, -15.9) * mm});
            skArc(sketch, "E12.19.4", {"start": v(20.57, -15.08) * mm, "mid": v(20.94, -15.75) * mm, "end": v(21.22, -16.45) * mm});
            skArc(sketch, "E12.19.5", {"start": v(19.66, -13.7) * mm, "mid": v(19.58, -14.06) * mm, "end": v(19.76, -14.38) * mm});
            skLineSegment(sketch, "E12.19.6", {"start": v(20.46, -14.95) * mm, "end": v(19.76, -14.38) * mm});
            skArc(sketch, "E12.19.7", {"start": v(18.98, -17) * mm, "mid": v(19.73, -17.22) * mm, "end": v(20.5, -17.35) * mm});
            skPoint(sketch, "E12.19.8", {"position": v(19.2, -13.92) * mm});
            skPoint(sketch, "E12.19.9", {"position": v(18.9, -16.96) * mm});
            skPoint(sketch, "E12.19.10", {"position": v(20.53, -15) * mm});
            skPoint(sketch, "E12.19.11", {"position": v(21.3, -16.7) * mm});
            skArc(sketch, "E12.19.12", {"start": v(21.15, -16.91) * mm, "mid": v(21.24, -16.7) * mm, "end": v(21.22, -16.45) * mm});
            skArc(sketch, "E12.19.13", {"start": v(20.5, -17.35) * mm, "mid": v(20.74, -17.32) * mm, "end": v(20.94, -17.18) * mm});
            skArc(sketch, "E12.19.14", {"start": v(18.84, -16.91) * mm, "mid": v(18.9, -16.96) * mm, "end": v(18.98, -17) * mm});
            skArc(sketch, "E12.19.15", {"start": v(20.57, -15.08) * mm, "mid": v(20.52, -15) * mm, "end": v(20.46, -14.95) * mm});
            skLineSegment(sketch, "E12.19.16", {"start": v(20.94, -17.18) * mm, "end": v(21.33, -16.75) * mm});
            skLineSegment(sketch, "E12.19.17", {"start": v(21.15, -16.91) * mm, "end": v(20.75, -17.46) * mm});
            skPoint(sketch, "E12.20.0", {"position": v(23.93, -12.67) * mm});
            skLineSegment(sketch, "E12.20.1", {"start": v(21.94, -12.62) * mm, "end": v(21.16, -12.23) * mm});
            skArc(sketch, "E12.20.2", {"start": v(21.16, -12.23) * mm, "mid": v(20.8, -12.19) * mm, "end": v(20.5, -12.4) * mm});
            skPoint(sketch, "E12.20.3", {"position": v(20.5, -11.9) * mm});
            skArc(sketch, "E12.20.4", {"start": v(23.26, -10.47) * mm, "mid": v(23.75, -11.05) * mm, "end": v(24.18, -11.68) * mm});
            skArc(sketch, "E12.20.5", {"start": v(22.08, -9.31) * mm, "mid": v(22.07, -9.68) * mm, "end": v(22.32, -9.96) * mm});
            skLineSegment(sketch, "E12.20.6", {"start": v(23.12, -10.37) * mm, "end": v(22.32, -9.96) * mm});
            skArc(sketch, "E12.20.7", {"start": v(22.1, -12.68) * mm, "mid": v(22.88, -12.74) * mm, "end": v(23.66, -12.7) * mm});
            skPoint(sketch, "E12.20.8", {"position": v(21.67, -9.62) * mm});
            skPoint(sketch, "E12.20.9", {"position": v(22.02, -12.66) * mm});
            skPoint(sketch, "E12.20.10", {"position": v(23.2, -10.4) * mm});
            skPoint(sketch, "E12.20.11", {"position": v(24.3, -11.91) * mm});
            skArc(sketch, "E12.20.12", {"start": v(24.2, -12.14) * mm, "mid": v(24.24, -11.91) * mm, "end": v(24.18, -11.68) * mm});
            skArc(sketch, "E12.20.13", {"start": v(23.66, -12.7) * mm, "mid": v(23.89, -12.63) * mm, "end": v(24.05, -12.45) * mm});
            skArc(sketch, "E12.20.14", {"start": v(21.94, -12.62) * mm, "mid": v(22.02, -12.66) * mm, "end": v(22.1, -12.68) * mm});
            skArc(sketch, "E12.20.15", {"start": v(23.26, -10.47) * mm, "mid": v(23.2, -10.41) * mm, "end": v(23.12, -10.37) * mm});
            skLineSegment(sketch, "E12.20.16", {"start": v(24.05, -12.45) * mm, "end": v(24.34, -11.95) * mm});
            skLineSegment(sketch, "E12.20.17", {"start": v(24.2, -12.14) * mm, "end": v(23.93, -12.77) * mm});
            skPoint(sketch, "E12.21.0", {"position": v(26.04, -7.42) * mm});
            skLineSegment(sketch, "E12.21.1", {"start": v(24.09, -7.79) * mm, "end": v(23.24, -7.56) * mm});
            skArc(sketch, "E12.21.2", {"start": v(23.24, -7.56) * mm, "mid": v(22.87, -7.6) * mm, "end": v(22.63, -7.88) * mm});
            skPoint(sketch, "E12.21.3", {"position": v(22.53, -7.37) * mm});
            skArc(sketch, "E12.21.4", {"start": v(24.93, -5.4) * mm, "mid": v(25.53, -5.87) * mm, "end": v(26.08, -6.4) * mm});
            skArc(sketch, "E12.21.5", {"start": v(23.53, -4.52) * mm, "mid": v(23.6, -4.88) * mm, "end": v(23.9, -5.1) * mm});
            skLineSegment(sketch, "E12.21.6", {"start": v(24.77, -5.33) * mm, "end": v(23.9, -5.1) * mm});
            skArc(sketch, "E12.21.7", {"start": v(24.25, -7.8) * mm, "mid": v(25.03, -7.7) * mm, "end": v(25.79, -7.5) * mm});
            skPoint(sketch, "E12.21.8", {"position": v(23.2, -4.9) * mm});
            skPoint(sketch, "E12.21.9", {"position": v(24.17, -7.8) * mm});
            skPoint(sketch, "E12.21.10", {"position": v(24.86, -5.36) * mm});
            skPoint(sketch, "E12.21.11", {"position": v(26.25, -6.6) * mm});
            skArc(sketch, "E12.21.12", {"start": v(26.2, -6.85) * mm, "mid": v(26.2, -6.6) * mm, "end": v(26.08, -6.4) * mm});
            skArc(sketch, "E12.21.13", {"start": v(25.79, -7.5) * mm, "mid": v(26, -7.38) * mm, "end": v(26.11, -7.18) * mm});
            skArc(sketch, "E12.21.14", {"start": v(24.09, -7.79) * mm, "mid": v(24.17, -7.8) * mm, "end": v(24.25, -7.8) * mm});
            skArc(sketch, "E12.21.15", {"start": v(24.93, -5.4) * mm, "mid": v(24.85, -5.36) * mm, "end": v(24.77, -5.33) * mm});
            skLineSegment(sketch, "E12.21.16", {"start": v(26.11, -7.18) * mm, "end": v(26.3, -6.63) * mm});
            skLineSegment(sketch, "E12.21.17", {"start": v(26.2, -6.85) * mm, "end": v(26.06, -7.51) * mm});
            skPoint(sketch, "E12.22.0", {"position": v(27.01, -1.85) * mm});
            skLineSegment(sketch, "E12.22.1", {"start": v(25.18, -2.6) * mm, "end": v(24.3, -2.56) * mm});
            skArc(sketch, "E12.22.2", {"start": v(24.3, -2.56) * mm, "mid": v(23.95, -2.68) * mm, "end": v(23.77, -3) * mm});
            skPoint(sketch, "E12.22.3", {"position": v(23.57, -2.52) * mm});
            skArc(sketch, "E12.22.4", {"start": v(25.5, -0.1) * mm, "mid": v(26.2, -0.43) * mm, "end": v(26.84, -0.84) * mm});
            skArc(sketch, "E12.22.5", {"start": v(23.96, 0.47) * mm, "mid": v(24.1, 0.13) * mm, "end": v(24.44, -0.02) * mm});
            skLineSegment(sketch, "E12.22.6", {"start": v(25.34, -0.07) * mm, "end": v(24.44, -0.02) * mm});
            skArc(sketch, "E12.22.7", {"start": v(25.35, -2.6) * mm, "mid": v(26.08, -2.33) * mm, "end": v(26.79, -1.98) * mm});
            skPoint(sketch, "E12.22.8", {"position": v(23.7, 0.02) * mm});
            skPoint(sketch, "E12.22.9", {"position": v(25.26, -2.61) * mm});
            skPoint(sketch, "E12.22.10", {"position": v(25.43, -0.07) * mm});
            skPoint(sketch, "E12.22.11", {"position": v(27.05, -1) * mm});
            skArc(sketch, "E12.22.12", {"start": v(27.05, -1.25) * mm, "mid": v(27, -1.02) * mm, "end": v(26.84, -0.84) * mm});
            skArc(sketch, "E12.22.13", {"start": v(26.79, -1.98) * mm, "mid": v(26.96, -1.82) * mm, "end": v(27.04, -1.6) * mm});
            skArc(sketch, "E12.22.14", {"start": v(25.18, -2.6) * mm, "mid": v(25.26, -2.6) * mm, "end": v(25.35, -2.6) * mm});
            skArc(sketch, "E12.22.15", {"start": v(25.5, -0.1) * mm, "mid": v(25.43, -0.08) * mm, "end": v(25.34, -0.07) * mm});
            skLineSegment(sketch, "E12.22.16", {"start": v(27.04, -1.6) * mm, "end": v(27.1, -1.02) * mm});
            skLineSegment(sketch, "E12.22.17", {"start": v(27.05, -1.25) * mm, "end": v(27.05, -1.93) * mm});
            skPoint(sketch, "E12.23.0", {"position": v(26.8, 3.81) * mm});
            skLineSegment(sketch, "E12.23.1", {"start": v(25.17, 2.68) * mm, "end": v(24.3, 2.55) * mm});
            skArc(sketch, "E12.23.2", {"start": v(24.3, 2.55) * mm, "mid": v(23.99, 2.36) * mm, "end": v(23.88, 2) * mm});
            skPoint(sketch, "E12.23.3", {"position": v(23.58, 2.43) * mm});
            skArc(sketch, "E12.23.4", {"start": v(24.97, 5.2) * mm, "mid": v(25.71, 5.03) * mm, "end": v(26.43, 4.76) * mm});
            skArc(sketch, "E12.23.5", {"start": v(23.34, 5.44) * mm, "mid": v(23.55, 5.14) * mm, "end": v(23.9, 5.06) * mm});
            skLineSegment(sketch, "E12.23.6", {"start": v(24.8, 5.2) * mm, "end": v(23.9, 5.06) * mm});
            skArc(sketch, "E12.23.7", {"start": v(25.33, 2.74) * mm, "mid": v(26, 3.14) * mm, "end": v(26.61, 3.63) * mm});
            skPoint(sketch, "E12.23.8", {"position": v(23.18, 4.95) * mm});
            skPoint(sketch, "E12.23.9", {"position": v(25.25, 2.7) * mm});
            skPoint(sketch, "E12.23.10", {"position": v(24.88, 5.22) * mm});
            skPoint(sketch, "E12.23.11", {"position": v(26.67, 4.65) * mm});
            skArc(sketch, "E12.23.12", {"start": v(26.72, 4.4) * mm, "mid": v(26.62, 4.61) * mm, "end": v(26.43, 4.76) * mm});
            skArc(sketch, "E12.23.13", {"start": v(26.61, 3.63) * mm, "mid": v(26.75, 3.83) * mm, "end": v(26.78, 4.06) * mm});
            skArc(sketch, "E12.23.14", {"start": v(25.17, 2.68) * mm, "mid": v(25.25, 2.7) * mm, "end": v(25.33, 2.74) * mm});
            skArc(sketch, "E12.23.15", {"start": v(24.97, 5.2) * mm, "mid": v(24.89, 5.21) * mm, "end": v(24.8, 5.2) * mm});
            skLineSegment(sketch, "E12.23.16", {"start": v(26.78, 4.06) * mm, "end": v(26.72, 4.64) * mm});
            skLineSegment(sketch, "E12.23.17", {"start": v(26.72, 4.4) * mm, "end": v(26.86, 3.74) * mm});
            skPoint(sketch, "E12.24.0", {"position": v(25.43, 9.3) * mm});
            skLineSegment(sketch, "E12.24.1", {"start": v(24.06, 7.86) * mm, "end": v(23.24, 7.54) * mm});
            skArc(sketch, "E12.24.2", {"start": v(23.24, 7.54) * mm, "mid": v(22.97, 7.3) * mm, "end": v(22.94, 6.93) * mm});
            skPoint(sketch, "E12.24.3", {"position": v(22.56, 7.28) * mm});
            skArc(sketch, "E12.24.4", {"start": v(23.34, 10.28) * mm, "mid": v(24.1, 10.26) * mm, "end": v(24.86, 10.15) * mm});
            skArc(sketch, "E12.24.5", {"start": v(21.7, 10.17) * mm, "mid": v(21.97, 9.92) * mm, "end": v(22.33, 9.92) * mm});
            skLineSegment(sketch, "E12.24.6", {"start": v(23.18, 10.25) * mm, "end": v(22.33, 9.92) * mm});
            skArc(sketch, "E12.24.7", {"start": v(24.2, 7.94) * mm, "mid": v(24.78, 8.48) * mm, "end": v(25.28, 9.08) * mm});
            skPoint(sketch, "E12.24.8", {"position": v(21.65, 9.66) * mm});
            skPoint(sketch, "E12.24.9", {"position": v(24.14, 7.89) * mm});
            skPoint(sketch, "E12.24.10", {"position": v(23.26, 10.28) * mm});
            skPoint(sketch, "E12.24.11", {"position": v(25.12, 10.1) * mm});
            skArc(sketch, "E12.24.12", {"start": v(25.22, 9.86) * mm, "mid": v(25.07, 10.05) * mm, "end": v(24.86, 10.15) * mm});
            skArc(sketch, "E12.24.13", {"start": v(25.28, 9.08) * mm, "mid": v(25.37, 9.3) * mm, "end": v(25.35, 9.54) * mm});
            skArc(sketch, "E12.24.14", {"start": v(24.06, 7.86) * mm, "mid": v(24.14, 7.9) * mm, "end": v(24.2, 7.94) * mm});
            skArc(sketch, "E12.24.15", {"start": v(23.34, 10.28) * mm, "mid": v(23.26, 10.27) * mm, "end": v(23.18, 10.25) * mm});
            skLineSegment(sketch, "E12.24.16", {"start": v(25.35, 9.54) * mm, "end": v(25.17, 10.1) * mm});
            skLineSegment(sketch, "E12.24.17", {"start": v(25.22, 9.86) * mm, "end": v(25.5, 9.24) * mm});
            skPoint(sketch, "E12.25.0", {"position": v(22.94, 14.38) * mm});
            skLineSegment(sketch, "E12.25.1", {"start": v(21.9, 12.7) * mm, "end": v(21.17, 12.21) * mm});
            skArc(sketch, "E12.25.2", {"start": v(21.17, 12.21) * mm, "mid": v(20.95, 11.91) * mm, "end": v(21, 11.55) * mm});
            skPoint(sketch, "E12.25.3", {"position": v(20.55, 11.81) * mm});
            skArc(sketch, "E12.25.4", {"start": v(20.7, 14.9) * mm, "mid": v(21.45, 15.05) * mm, "end": v(22.2, 15.1) * mm});
            skArc(sketch, "E12.25.5", {"start": v(19.1, 14.46) * mm, "mid": v(19.42, 14.27) * mm, "end": v(19.78, 14.35) * mm});
            skLineSegment(sketch, "E12.25.6", {"start": v(20.54, 14.84) * mm, "end": v(19.78, 14.35) * mm});
            skArc(sketch, "E12.25.7", {"start": v(22.03, 12.8) * mm, "mid": v(22.47, 13.45) * mm, "end": v(22.83, 14.14) * mm});
            skPoint(sketch, "E12.25.8", {"position": v(19.17, 13.95) * mm});
            skPoint(sketch, "E12.25.9", {"position": v(21.97, 12.74) * mm});
            skPoint(sketch, "E12.25.10", {"position": v(20.61, 14.89) * mm});
            skPoint(sketch, "E12.25.11", {"position": v(22.47, 15.1) * mm});
            skArc(sketch, "E12.25.12", {"start": v(22.62, 14.89) * mm, "mid": v(22.44, 15.04) * mm, "end": v(22.2, 15.1) * mm});
            skArc(sketch, "E12.25.13", {"start": v(22.83, 14.14) * mm, "mid": v(22.88, 14.37) * mm, "end": v(22.81, 14.6) * mm});
            skArc(sketch, "E12.25.14", {"start": v(21.9, 12.7) * mm, "mid": v(21.97, 12.74) * mm, "end": v(22.03, 12.8) * mm});
            skArc(sketch, "E12.25.15", {"start": v(20.7, 14.9) * mm, "mid": v(20.62, 14.88) * mm, "end": v(20.54, 14.84) * mm});
            skLineSegment(sketch, "E12.25.16", {"start": v(22.81, 14.6) * mm, "end": v(22.52, 15.1) * mm});
            skLineSegment(sketch, "E12.25.17", {"start": v(22.62, 14.89) * mm, "end": v(23.02, 14.34) * mm});
            skPoint(sketch, "E12.26.0", {"position": v(19.44, 18.84) * mm});
            skLineSegment(sketch, "E12.26.1", {"start": v(18.79, 16.97) * mm, "end": v(18.17, 16.34) * mm});
            skArc(sketch, "E12.26.2", {"start": v(18.17, 16.34) * mm, "mid": v(18.02, 16) * mm, "end": v(18.14, 15.66) * mm});
            skPoint(sketch, "E12.26.3", {"position": v(17.65, 15.83) * mm});
            skArc(sketch, "E12.26.4", {"start": v(17.14, 18.89) * mm, "mid": v(17.85, 19.18) * mm, "end": v(18.58, 19.38) * mm});
            skArc(sketch, "E12.26.5", {"start": v(15.68, 18.12) * mm, "mid": v(16.03, 18) * mm, "end": v(16.37, 18.15) * mm});
            skLineSegment(sketch, "E12.26.6", {"start": v(17, 18.79) * mm, "end": v(16.37, 18.15) * mm});
            skArc(sketch, "E12.26.7", {"start": v(18.88, 17.1) * mm, "mid": v(19.19, 17.83) * mm, "end": v(19.4, 18.58) * mm});
            skPoint(sketch, "E12.26.8", {"position": v(15.85, 17.63) * mm});
            skPoint(sketch, "E12.26.9", {"position": v(18.85, 17.03) * mm});
            skPoint(sketch, "E12.26.10", {"position": v(17.07, 18.85) * mm});
            skPoint(sketch, "E12.26.11", {"position": v(18.84, 19.43) * mm});
            skArc(sketch, "E12.26.12", {"start": v(19.03, 19.26) * mm, "mid": v(18.82, 19.38) * mm, "end": v(18.58, 19.38) * mm});
            skArc(sketch, "E12.26.13", {"start": v(19.4, 18.58) * mm, "mid": v(19.39, 18.82) * mm, "end": v(19.28, 19.03) * mm});
            skArc(sketch, "E12.26.14", {"start": v(18.79, 16.97) * mm, "mid": v(18.84, 17.03) * mm, "end": v(18.88, 17.1) * mm});
            skArc(sketch, "E12.26.15", {"start": v(17.14, 18.89) * mm, "mid": v(17.07, 18.84) * mm, "end": v(17, 18.79) * mm});
            skLineSegment(sketch, "E12.26.16", {"start": v(19.28, 19.03) * mm, "end": v(18.89, 19.46) * mm});
            skLineSegment(sketch, "E12.26.17", {"start": v(19.03, 19.26) * mm, "end": v(19.53, 18.8) * mm});
            skPoint(sketch, "E12.27.0", {"position": v(15.1, 22.47) * mm});
            skLineSegment(sketch, "E12.27.1", {"start": v(14.85, 20.5) * mm, "end": v(14.37, 19.76) * mm});
            skArc(sketch, "E12.27.2", {"start": v(14.37, 19.76) * mm, "mid": v(14.3, 19.4) * mm, "end": v(14.48, 19.09) * mm});
            skPoint(sketch, "E12.27.3", {"position": v(13.97, 19.15) * mm});
            skArc(sketch, "E12.27.4", {"start": v(12.84, 22.04) * mm, "mid": v(13.47, 22.47) * mm, "end": v(14.15, 22.82) * mm});
            skArc(sketch, "E12.27.5", {"start": v(11.57, 20.98) * mm, "mid": v(11.94, 20.94) * mm, "end": v(12.24, 21.16) * mm});
            skLineSegment(sketch, "E12.27.6", {"start": v(12.73, 21.91) * mm, "end": v(12.24, 21.16) * mm});
            skArc(sketch, "E12.27.7", {"start": v(14.92, 20.65) * mm, "mid": v(15.06, 21.42) * mm, "end": v(15.1, 22.2) * mm});
            skPoint(sketch, "E12.27.8", {"position": v(11.84, 20.54) * mm});
            skPoint(sketch, "E12.27.9", {"position": v(14.9, 20.57) * mm});
            skPoint(sketch, "E12.27.10", {"position": v(12.77, 21.98) * mm});
            skPoint(sketch, "E12.27.11", {"position": v(14.39, 22.93) * mm});
            skArc(sketch, "E12.27.12", {"start": v(14.6, 22.8) * mm, "mid": v(14.38, 22.87) * mm, "end": v(14.15, 22.82) * mm});
            skArc(sketch, "E12.27.13", {"start": v(15.1, 22.2) * mm, "mid": v(15.05, 22.44) * mm, "end": v(14.9, 22.62) * mm});
            skArc(sketch, "E12.27.14", {"start": v(14.85, 20.5) * mm, "mid": v(14.89, 20.58) * mm, "end": v(14.92, 20.65) * mm});
            skArc(sketch, "E12.27.15", {"start": v(12.84, 22.04) * mm, "mid": v(12.78, 21.98) * mm, "end": v(12.73, 21.91) * mm});
            skLineSegment(sketch, "E12.27.16", {"start": v(14.9, 22.62) * mm, "end": v(14.43, 22.96) * mm});
            skLineSegment(sketch, "E12.27.17", {"start": v(14.6, 22.8) * mm, "end": v(15.2, 22.46) * mm});
            skPoint(sketch, "E12.28.0", {"position": v(10.1, 25.12) * mm});
            skLineSegment(sketch, "E12.28.1", {"start": v(10.26, 23.14) * mm, "end": v(9.95, 22.32) * mm});
            skArc(sketch, "E12.28.2", {"start": v(9.95, 22.32) * mm, "mid": v(9.95, 21.95) * mm, "end": v(10.2, 21.68) * mm});
            skPoint(sketch, "E12.28.3", {"position": v(9.68, 21.64) * mm});
            skArc(sketch, "E12.28.4", {"start": v(7.98, 24.23) * mm, "mid": v(8.5, 24.78) * mm, "end": v(9.1, 25.27) * mm});
            skArc(sketch, "E12.28.5", {"start": v(6.96, 22.93) * mm, "mid": v(7.32, 22.96) * mm, "end": v(7.57, 23.24) * mm});
            skLineSegment(sketch, "E12.28.6", {"start": v(7.9, 24.08) * mm, "end": v(7.57, 23.24) * mm});
            skArc(sketch, "E12.28.7", {"start": v(10.3, 23.3) * mm, "mid": v(10.28, 24.09) * mm, "end": v(10.16, 24.86) * mm});
            skPoint(sketch, "E12.28.8", {"position": v(7.3, 22.55) * mm});
            skPoint(sketch, "E12.28.9", {"position": v(10.3, 23.22) * mm});
            skPoint(sketch, "E12.28.10", {"position": v(7.92, 24.16) * mm});
            skPoint(sketch, "E12.28.11", {"position": v(9.3, 25.42) * mm});
            skArc(sketch, "E12.28.12", {"start": v(9.55, 25.34) * mm, "mid": v(9.31, 25.36) * mm, "end": v(9.1, 25.27) * mm});
            skArc(sketch, "E12.28.13", {"start": v(10.16, 24.86) * mm, "mid": v(10.06, 25.08) * mm, "end": v(9.87, 25.22) * mm});
            skArc(sketch, "E12.28.14", {"start": v(10.26, 23.14) * mm, "mid": v(10.29, 23.22) * mm, "end": v(10.3, 23.3) * mm});
            skArc(sketch, "E12.28.15", {"start": v(7.98, 24.23) * mm, "mid": v(7.93, 24.16) * mm, "end": v(7.9, 24.08) * mm});
            skLineSegment(sketch, "E12.28.16", {"start": v(9.87, 25.22) * mm, "end": v(9.34, 25.46) * mm});
            skLineSegment(sketch, "E12.28.17", {"start": v(9.55, 25.34) * mm, "end": v(10.2, 25.13) * mm});
            skPoint(sketch, "E12.29.0", {"position": v(4.66, 26.67) * mm});
            skLineSegment(sketch, "E12.29.1", {"start": v(5.23, 24.77) * mm, "end": v(5.09, 23.9) * mm});
            skArc(sketch, "E12.29.2", {"start": v(5.09, 23.9) * mm, "mid": v(5.17, 23.54) * mm, "end": v(5.47, 23.33) * mm});
            skPoint(sketch, "E12.29.3", {"position": v(4.97, 23.18) * mm});
            skArc(sketch, "E12.29.4", {"start": v(2.77, 25.36) * mm, "mid": v(3.17, 26) * mm, "end": v(3.64, 26.6) * mm});
            skArc(sketch, "E12.29.5", {"start": v(2.04, 23.88) * mm, "mid": v(2.39, 23.98) * mm, "end": v(2.57, 24.3) * mm});
            skLineSegment(sketch, "E12.29.6", {"start": v(2.71, 25.2) * mm, "end": v(2.57, 24.3) * mm});
            skArc(sketch, "E12.29.7", {"start": v(5.23, 24.94) * mm, "mid": v(5.04, 25.7) * mm, "end": v(4.77, 26.43) * mm});
            skPoint(sketch, "E12.29.8", {"position": v(2.46, 23.58) * mm});
            skPoint(sketch, "E12.29.9", {"position": v(5.24, 24.85) * mm});
            skPoint(sketch, "E12.29.10", {"position": v(2.73, 25.28) * mm});
            skPoint(sketch, "E12.29.11", {"position": v(3.82, 26.8) * mm});
            skArc(sketch, "E12.29.12", {"start": v(4.07, 26.77) * mm, "mid": v(3.84, 26.74) * mm, "end": v(3.64, 26.6) * mm});
            skArc(sketch, "E12.29.13", {"start": v(4.77, 26.43) * mm, "mid": v(4.63, 26.62) * mm, "end": v(4.41, 26.72) * mm});
            skArc(sketch, "E12.29.14", {"start": v(5.23, 24.77) * mm, "mid": v(5.23, 24.85) * mm, "end": v(5.23, 24.94) * mm});
            skArc(sketch, "E12.29.15", {"start": v(2.77, 25.36) * mm, "mid": v(2.73, 25.28) * mm, "end": v(2.71, 25.2) * mm});
            skLineSegment(sketch, "E12.29.16", {"start": v(4.41, 26.72) * mm, "end": v(3.84, 26.84) * mm});
            skLineSegment(sketch, "E12.29.17", {"start": v(4.07, 26.77) * mm, "end": v(4.75, 26.7) * mm});
            skPoint(sketch, "E12.center", {"position": v(0, 0) * mm});
            skLineSegment(sketch, "E13", {"start": v(0.5, 23.96) * mm, "end": v(2.04, 23.88) * mm});
            skLineSegment(sketch, "E14.1.0", {"start": v(-4.5, 23.54) * mm, "end": v(-2.97, 23.78) * mm});
            skLineSegment(sketch, "E14.2.0", {"start": v(-9.29, 22.09) * mm, "end": v(-7.85, 22.64) * mm});
            skLineSegment(sketch, "E14.3.0", {"start": v(-13.68, 19.67) * mm, "end": v(-12.39, 20.51) * mm});
            skLineSegment(sketch, "E14.4.0", {"start": v(-17.47, 16.4) * mm, "end": v(-16.38, 17.49) * mm});
            skLineSegment(sketch, "E14.5.0", {"start": v(-20.5, 12.4) * mm, "end": v(-19.66, 13.7) * mm});
            skLineSegment(sketch, "E14.6.0", {"start": v(-22.63, 7.88) * mm, "end": v(-22.08, 9.31) * mm});
            skLineSegment(sketch, "E14.7.0", {"start": v(-23.77, 3) * mm, "end": v(-23.53, 4.52) * mm});
            skLineSegment(sketch, "E14.8.0", {"start": v(-23.88, -2) * mm, "end": v(-23.96, -0.47) * mm});
            skLineSegment(sketch, "E14.9.0", {"start": v(-22.94, -6.93) * mm, "end": v(-23.34, -5.44) * mm});
            skLineSegment(sketch, "E14.10.0", {"start": v(-21, -11.55) * mm, "end": v(-21.7, -10.17) * mm});
            skLineSegment(sketch, "E14.11.0", {"start": v(-18.14, -15.66) * mm, "end": v(-19.1, -14.46) * mm});
            skLineSegment(sketch, "E14.12.0", {"start": v(-14.48, -19.09) * mm, "end": v(-15.68, -18.12) * mm});
            skLineSegment(sketch, "E14.13.0", {"start": v(-10.2, -21.68) * mm, "end": v(-11.57, -20.98) * mm});
            skLineSegment(sketch, "E14.14.0", {"start": v(-5.47, -23.33) * mm, "end": v(-6.96, -22.93) * mm});
            skLineSegment(sketch, "E14.15.0", {"start": v(-0.5, -23.96) * mm, "end": v(-2.04, -23.88) * mm});
            skLineSegment(sketch, "E14.16.0", {"start": v(4.5, -23.54) * mm, "end": v(2.97, -23.78) * mm});
            skLineSegment(sketch, "E14.17.0", {"start": v(9.29, -22.09) * mm, "end": v(7.85, -22.64) * mm});
            skLineSegment(sketch, "E14.18.0", {"start": v(13.68, -19.67) * mm, "end": v(12.39, -20.51) * mm});
            skLineSegment(sketch, "E14.19.0", {"start": v(17.47, -16.4) * mm, "end": v(16.38, -17.49) * mm});
            skLineSegment(sketch, "E14.20.0", {"start": v(20.5, -12.4) * mm, "end": v(19.66, -13.7) * mm});
            skLineSegment(sketch, "E14.21.0", {"start": v(22.63, -7.88) * mm, "end": v(22.08, -9.31) * mm});
            skLineSegment(sketch, "E14.22.0", {"start": v(23.77, -3) * mm, "end": v(23.53, -4.52) * mm});
            skLineSegment(sketch, "E14.23.0", {"start": v(23.88, 2) * mm, "end": v(23.96, 0.47) * mm});
            skLineSegment(sketch, "E14.24.0", {"start": v(22.94, 6.93) * mm, "end": v(23.34, 5.44) * mm});
            skLineSegment(sketch, "E14.25.0", {"start": v(21, 11.55) * mm, "end": v(21.7, 10.17) * mm});
            skLineSegment(sketch, "E14.26.0", {"start": v(18.14, 15.66) * mm, "end": v(19.1, 14.46) * mm});
            skLineSegment(sketch, "E14.27.0", {"start": v(14.48, 19.09) * mm, "end": v(15.68, 18.12) * mm});
            skLineSegment(sketch, "E14.28.0", {"start": v(10.2, 21.68) * mm, "end": v(11.57, 20.98) * mm});
            skLineSegment(sketch, "E14.29.0", {"start": v(5.47, 23.33) * mm, "end": v(6.96, 22.93) * mm});
            skSolve(sketch);
        }
        {
            var Q0;
            Q0=qCreatedBy(makeId("Front.planeOp"),FACE);
            cPlane(context, id + "F1", {"entities" : qUnion([Q0]), "cplaneType" : CPlaneType.OFFSET, "offset" : 22 * mm, "oppositeDirection" : true, "width" : 152.4 * mm, "height" : 152.4 * mm});
        }
        {
            var Q0;
            Q0=qCreatedBy(id+"F1.planeOp",FACE);
            var sketch = newSketch(context, id + "F2", { "sketchPlane" : qUnion([Q0])});
            skArc(sketch, "E15", {"start": v(-0.1, 38.37) * mm, "mid": v(-0.63, 39.42) * mm, "end": v(-1.27, 40.4) * mm});
            skLineSegment(sketch, "E16", {"start": v(-1.7, 40.6) * mm, "end": v(-2.13, 40.58) * mm});
            skLineSegment(sketch, "E17", {"start": v(0.01, 37.84) * mm, "end": v(0.1, 36.04) * mm});
            skLineSegment(sketch, "E18.MirrorCS", {"start": v(-2.55, 40.56) * mm, "end": v(-2.13, 40.58) * mm});
            skArc(sketch, "E19.MirrorCS", {"start": v(-3.9, 38.17) * mm, "mid": v(-3.5, 39.27) * mm, "end": v(-2.96, 40.3) * mm});
            skLineSegment(sketch, "E20.MirrorCS", {"start": v(-3.97, 37.63) * mm, "end": v(-3.87, 35.83) * mm});
            skPoint(sketch, "E21.visualSharp", {"position": v(0, 38.1) * mm});
            skArc(sketch, "E21.filletArc", {"start": v(0.01, 37.84) * mm, "mid": v(-0.02, 38.1) * mm, "end": v(-0.1, 38.37) * mm});
            skPoint(sketch, "E22.visualSharp", {"position": v(-3.98, 37.9) * mm});
            skArc(sketch, "E22.filletArc", {"start": v(-3.9, 38.17) * mm, "mid": v(-3.96, 37.9) * mm, "end": v(-3.97, 37.63) * mm});
            skPoint(sketch, "E23.visualSharp", {"position": v(-1.44, 40.61) * mm});
            skArc(sketch, "E23.filletArc", {"start": v(-1.27, 40.4) * mm, "mid": v(-1.46, 40.55) * mm, "end": v(-1.7, 40.6) * mm});
            skPoint(sketch, "E24.visualSharp", {"position": v(-2.81, 40.54) * mm});
            skArc(sketch, "E24.filletArc", {"start": v(-2.55, 40.56) * mm, "mid": v(-2.78, 40.48) * mm, "end": v(-2.96, 40.3) * mm});
            skPoint(sketch, "E25.visualSharp", {"position": v(-3.85, 35.35) * mm});
            skArc(sketch, "E25.filletArc", {"start": v(-4.32, 35.3) * mm, "mid": v(-4, 35.47) * mm, "end": v(-3.87, 35.83) * mm});
            skPoint(sketch, "E26.visualSharp", {"position": v(0.13, 35.56) * mm});
            skArc(sketch, "E26.filletArc", {"start": v(0.1, 36.04) * mm, "mid": v(0.26, 35.7) * mm, "end": v(0.6, 35.55) * mm});
            skPoint(sketch, "E27.1.0", {"position": v(-11.18, 39.07) * mm});
            skPoint(sketch, "E27.1.1", {"position": v(-11.77, 36.24) * mm});
            skArc(sketch, "E27.1.2", {"start": v(-11.75, 36.52) * mm, "mid": v(-11.58, 37.68) * mm, "end": v(-11.27, 38.81) * mm});
            skPoint(sketch, "E27.1.3", {"position": v(-11.12, 33.78) * mm});
            skPoint(sketch, "E27.1.4", {"position": v(-7.26, 34.81) * mm});
            skLineSegment(sketch, "E27.1.5", {"start": v(-11.7, 35.98) * mm, "end": v(-11.24, 34.24) * mm});
            skPoint(sketch, "E27.1.6", {"position": v(-9.85, 39.43) * mm});
            skLineSegment(sketch, "E27.1.7", {"start": v(-7.85, 37.01) * mm, "end": v(-7.39, 35.27) * mm});
            skArc(sketch, "E27.1.8", {"start": v(-8.08, 37.5) * mm, "mid": v(-8.8, 38.43) * mm, "end": v(-9.64, 39.25) * mm});
            skPoint(sketch, "E27.1.9", {"position": v(-7.92, 37.27) * mm});
            skArc(sketch, "E27.1.10", {"start": v(-11.56, 33.63) * mm, "mid": v(-11.28, 33.87) * mm, "end": v(-11.24, 34.24) * mm});
            skArc(sketch, "E27.1.11", {"start": v(-7.39, 35.27) * mm, "mid": v(-7.16, 34.97) * mm, "end": v(-6.8, 34.9) * mm});
            skArc(sketch, "E27.1.12", {"start": v(-7.85, 37.01) * mm, "mid": v(-7.95, 37.27) * mm, "end": v(-8.08, 37.5) * mm});
            skArc(sketch, "E27.1.13", {"start": v(-10.92, 39.14) * mm, "mid": v(-11.14, 39.02) * mm, "end": v(-11.27, 38.81) * mm});
            skArc(sketch, "E27.1.14", {"start": v(-9.64, 39.25) * mm, "mid": v(-9.86, 39.36) * mm, "end": v(-10.1, 39.36) * mm});
            skArc(sketch, "E27.1.15", {"start": v(-11.75, 36.52) * mm, "mid": v(-11.75, 36.25) * mm, "end": v(-11.7, 35.98) * mm});
            skLineSegment(sketch, "E27.1.16", {"start": v(-10.92, 39.14) * mm, "end": v(-10.52, 39.25) * mm});
            skLineSegment(sketch, "E27.1.17", {"start": v(-10.1, 39.36) * mm, "end": v(-10.52, 39.25) * mm});
            skPoint(sketch, "E27.2.0", {"position": v(-19.06, 35.9) * mm});
            skPoint(sketch, "E27.2.1", {"position": v(-19.05, 33) * mm});
            skArc(sketch, "E27.2.2", {"start": v(-19.1, 33.28) * mm, "mid": v(-19.17, 34.45) * mm, "end": v(-19.1, 35.62) * mm});
            skPoint(sketch, "E27.2.3", {"position": v(-17.9, 30.73) * mm});
            skPoint(sketch, "E27.2.4", {"position": v(-14.34, 32.54) * mm});
            skLineSegment(sketch, "E27.2.5", {"start": v(-18.93, 32.76) * mm, "end": v(-18.11, 31.15) * mm});
            skPoint(sketch, "E27.2.6", {"position": v(-17.83, 36.52) * mm});
            skLineSegment(sketch, "E27.2.7", {"start": v(-15.38, 34.57) * mm, "end": v(-14.56, 32.96) * mm});
            skArc(sketch, "E27.2.8", {"start": v(-15.7, 35) * mm, "mid": v(-16.6, 35.76) * mm, "end": v(-17.6, 36.39) * mm});
            skPoint(sketch, "E27.2.9", {"position": v(-15.5, 34.8) * mm});
            skArc(sketch, "E27.2.10", {"start": v(-18.3, 30.49) * mm, "mid": v(-18.08, 30.78) * mm, "end": v(-18.11, 31.15) * mm});
            skArc(sketch, "E27.2.11", {"start": v(-14.56, 32.96) * mm, "mid": v(-14.28, 32.72) * mm, "end": v(-13.9, 32.73) * mm});
            skArc(sketch, "E27.2.12", {"start": v(-15.38, 34.57) * mm, "mid": v(-15.52, 34.8) * mm, "end": v(-15.7, 35) * mm});
            skArc(sketch, "E27.2.13", {"start": v(-18.82, 36.01) * mm, "mid": v(-19, 35.85) * mm, "end": v(-19.1, 35.62) * mm});
            skArc(sketch, "E27.2.14", {"start": v(-17.6, 36.39) * mm, "mid": v(-17.83, 36.45) * mm, "end": v(-18.07, 36.4) * mm});
            skArc(sketch, "E27.2.15", {"start": v(-19.1, 33.28) * mm, "mid": v(-19.03, 33.01) * mm, "end": v(-18.93, 32.76) * mm});
            skLineSegment(sketch, "E27.2.16", {"start": v(-18.82, 36.01) * mm, "end": v(-18.45, 36.2) * mm});
            skLineSegment(sketch, "E27.2.17", {"start": v(-18.07, 36.4) * mm, "end": v(-18.45, 36.2) * mm});
            skPoint(sketch, "E27.3.0", {"position": v(-26.1, 31.15) * mm});
            skPoint(sketch, "E27.3.1", {"position": v(-25.5, 28.31) * mm});
            skArc(sketch, "E27.3.2", {"start": v(-25.6, 28.59) * mm, "mid": v(-25.91, 29.71) * mm, "end": v(-26.09, 30.87) * mm});
            skPoint(sketch, "E27.3.3", {"position": v(-23.9, 26.34) * mm});
            skPoint(sketch, "E27.3.4", {"position": v(-20.8, 28.85) * mm});
            skLineSegment(sketch, "E27.3.5", {"start": v(-25.33, 28.1) * mm, "end": v(-24.2, 26.7) * mm});
            skPoint(sketch, "E27.3.6", {"position": v(-25.04, 32.01) * mm});
            skLineSegment(sketch, "E27.3.7", {"start": v(-22.23, 30.62) * mm, "end": v(-21.1, 29.22) * mm});
            skArc(sketch, "E27.3.8", {"start": v(-22.64, 30.98) * mm, "mid": v(-23.68, 31.52) * mm, "end": v(-24.77, 31.94) * mm});
            skPoint(sketch, "E27.3.9", {"position": v(-22.4, 30.82) * mm});
            skArc(sketch, "E27.3.10", {"start": v(-24.24, 26.02) * mm, "mid": v(-24.08, 26.35) * mm, "end": v(-24.2, 26.7) * mm});
            skArc(sketch, "E27.3.11", {"start": v(-21.1, 29.22) * mm, "mid": v(-20.77, 29.03) * mm, "end": v(-20.4, 29.12) * mm});
            skArc(sketch, "E27.3.12", {"start": v(-22.23, 30.62) * mm, "mid": v(-22.42, 30.82) * mm, "end": v(-22.64, 30.98) * mm});
            skArc(sketch, "E27.3.13", {"start": v(-25.9, 31.31) * mm, "mid": v(-26.05, 31.12) * mm, "end": v(-26.09, 30.87) * mm});
            skArc(sketch, "E27.3.14", {"start": v(-24.77, 31.94) * mm, "mid": v(-25.02, 31.95) * mm, "end": v(-25.24, 31.84) * mm});
            skArc(sketch, "E27.3.15", {"start": v(-25.6, 28.59) * mm, "mid": v(-25.48, 28.34) * mm, "end": v(-25.33, 28.1) * mm});
            skLineSegment(sketch, "E27.3.16", {"start": v(-25.9, 31.31) * mm, "end": v(-25.57, 31.58) * mm});
            skLineSegment(sketch, "E27.3.17", {"start": v(-25.24, 31.84) * mm, "end": v(-25.57, 31.58) * mm});
            skPoint(sketch, "E27.4.0", {"position": v(-32.01, 25.04) * mm});
            skPoint(sketch, "E27.4.1", {"position": v(-30.82, 22.4) * mm});
            skArc(sketch, "E27.4.2", {"start": v(-30.98, 22.64) * mm, "mid": v(-31.52, 23.68) * mm, "end": v(-31.94, 24.77) * mm});
            skPoint(sketch, "E27.4.3", {"position": v(-28.85, 20.8) * mm});
            skPoint(sketch, "E27.4.4", {"position": v(-26.34, 23.9) * mm});
            skLineSegment(sketch, "E27.4.5", {"start": v(-30.62, 22.23) * mm, "end": v(-29.22, 21.1) * mm});
            skPoint(sketch, "E27.4.6", {"position": v(-31.15, 26.1) * mm});
            skLineSegment(sketch, "E27.4.7", {"start": v(-28.1, 25.33) * mm, "end": v(-26.7, 24.2) * mm});
            skArc(sketch, "E27.4.8", {"start": v(-28.59, 25.6) * mm, "mid": v(-29.71, 25.91) * mm, "end": v(-30.87, 26.09) * mm});
            skPoint(sketch, "E27.4.9", {"position": v(-28.31, 25.5) * mm});
            skArc(sketch, "E27.4.10", {"start": v(-29.12, 20.4) * mm, "mid": v(-29.03, 20.77) * mm, "end": v(-29.22, 21.1) * mm});
            skArc(sketch, "E27.4.11", {"start": v(-26.7, 24.2) * mm, "mid": v(-26.35, 24.08) * mm, "end": v(-26.02, 24.24) * mm});
            skArc(sketch, "E27.4.12", {"start": v(-28.1, 25.33) * mm, "mid": v(-28.34, 25.48) * mm, "end": v(-28.59, 25.6) * mm});
            skArc(sketch, "E27.4.13", {"start": v(-31.84, 25.24) * mm, "mid": v(-31.95, 25.02) * mm, "end": v(-31.94, 24.77) * mm});
            skArc(sketch, "E27.4.14", {"start": v(-30.87, 26.09) * mm, "mid": v(-31.12, 26.05) * mm, "end": v(-31.31, 25.9) * mm});
            skArc(sketch, "E27.4.15", {"start": v(-30.98, 22.64) * mm, "mid": v(-30.82, 22.42) * mm, "end": v(-30.62, 22.23) * mm});
            skLineSegment(sketch, "E27.4.16", {"start": v(-31.84, 25.24) * mm, "end": v(-31.58, 25.57) * mm});
            skLineSegment(sketch, "E27.4.17", {"start": v(-31.31, 25.9) * mm, "end": v(-31.58, 25.57) * mm});
            skPoint(sketch, "E27.5.0", {"position": v(-36.52, 17.83) * mm});
            skPoint(sketch, "E27.5.1", {"position": v(-34.8, 15.5) * mm});
            skArc(sketch, "E27.5.2", {"start": v(-35, 15.7) * mm, "mid": v(-35.76, 16.6) * mm, "end": v(-36.39, 17.6) * mm});
            skPoint(sketch, "E27.5.3", {"position": v(-32.54, 14.34) * mm});
            skPoint(sketch, "E27.5.4", {"position": v(-30.73, 17.9) * mm});
            skLineSegment(sketch, "E27.5.5", {"start": v(-34.57, 15.38) * mm, "end": v(-32.96, 14.56) * mm});
            skPoint(sketch, "E27.5.6", {"position": v(-35.9, 19.06) * mm});
            skLineSegment(sketch, "E27.5.7", {"start": v(-32.76, 18.93) * mm, "end": v(-31.15, 18.11) * mm});
            skArc(sketch, "E27.5.8", {"start": v(-33.28, 19.1) * mm, "mid": v(-34.45, 19.17) * mm, "end": v(-35.62, 19.1) * mm});
            skPoint(sketch, "E27.5.9", {"position": v(-33, 19.05) * mm});
            skArc(sketch, "E27.5.10", {"start": v(-32.73, 13.9) * mm, "mid": v(-32.72, 14.28) * mm, "end": v(-32.96, 14.56) * mm});
            skArc(sketch, "E27.5.11", {"start": v(-31.15, 18.11) * mm, "mid": v(-30.78, 18.08) * mm, "end": v(-30.49, 18.3) * mm});
            skArc(sketch, "E27.5.12", {"start": v(-32.76, 18.93) * mm, "mid": v(-33.01, 19.03) * mm, "end": v(-33.28, 19.1) * mm});
            skArc(sketch, "E27.5.13", {"start": v(-36.4, 18.07) * mm, "mid": v(-36.45, 17.83) * mm, "end": v(-36.39, 17.6) * mm});
            skArc(sketch, "E27.5.14", {"start": v(-35.62, 19.1) * mm, "mid": v(-35.85, 19) * mm, "end": v(-36.01, 18.82) * mm});
            skArc(sketch, "E27.5.15", {"start": v(-35, 15.7) * mm, "mid": v(-34.8, 15.52) * mm, "end": v(-34.57, 15.38) * mm});
            skLineSegment(sketch, "E27.5.16", {"start": v(-36.4, 18.07) * mm, "end": v(-36.2, 18.45) * mm});
            skLineSegment(sketch, "E27.5.17", {"start": v(-36.01, 18.82) * mm, "end": v(-36.2, 18.45) * mm});
            skPoint(sketch, "E27.6.0", {"position": v(-39.43, 9.85) * mm});
            skPoint(sketch, "E27.6.1", {"position": v(-37.27, 7.92) * mm});
            skArc(sketch, "E27.6.2", {"start": v(-37.5, 8.08) * mm, "mid": v(-38.43, 8.8) * mm, "end": v(-39.25, 9.64) * mm});
            skPoint(sketch, "E27.6.3", {"position": v(-34.81, 7.26) * mm});
            skPoint(sketch, "E27.6.4", {"position": v(-33.78, 11.12) * mm});
            skLineSegment(sketch, "E27.6.5", {"start": v(-37.01, 7.85) * mm, "end": v(-35.27, 7.39) * mm});
            skPoint(sketch, "E27.6.6", {"position": v(-39.07, 11.18) * mm});
            skLineSegment(sketch, "E27.6.7", {"start": v(-35.98, 11.7) * mm, "end": v(-34.24, 11.24) * mm});
            skArc(sketch, "E27.6.8", {"start": v(-36.52, 11.75) * mm, "mid": v(-37.68, 11.58) * mm, "end": v(-38.81, 11.27) * mm});
            skPoint(sketch, "E27.6.9", {"position": v(-36.24, 11.77) * mm});
            skArc(sketch, "E27.6.10", {"start": v(-34.9, 6.8) * mm, "mid": v(-34.97, 7.16) * mm, "end": v(-35.27, 7.39) * mm});
            skArc(sketch, "E27.6.11", {"start": v(-34.24, 11.24) * mm, "mid": v(-33.87, 11.28) * mm, "end": v(-33.63, 11.56) * mm});
            skArc(sketch, "E27.6.12", {"start": v(-35.98, 11.7) * mm, "mid": v(-36.25, 11.75) * mm, "end": v(-36.52, 11.75) * mm});
            skArc(sketch, "E27.6.13", {"start": v(-39.36, 10.1) * mm, "mid": v(-39.36, 9.86) * mm, "end": v(-39.25, 9.64) * mm});
            skArc(sketch, "E27.6.14", {"start": v(-38.81, 11.27) * mm, "mid": v(-39.02, 11.14) * mm, "end": v(-39.14, 10.92) * mm});
            skArc(sketch, "E27.6.15", {"start": v(-37.5, 8.08) * mm, "mid": v(-37.27, 7.95) * mm, "end": v(-37.01, 7.85) * mm});
            skLineSegment(sketch, "E27.6.16", {"start": v(-39.36, 10.1) * mm, "end": v(-39.25, 10.52) * mm});
            skLineSegment(sketch, "E27.6.17", {"start": v(-39.14, 10.92) * mm, "end": v(-39.25, 10.52) * mm});
            skPoint(sketch, "E27.7.0", {"position": v(-40.61, 1.44) * mm});
            skPoint(sketch, "E27.7.1", {"position": v(-38.1, 0) * mm});
            skArc(sketch, "E27.7.2", {"start": v(-38.37, 0.1) * mm, "mid": v(-39.42, 0.63) * mm, "end": v(-40.4, 1.27) * mm});
            skPoint(sketch, "E27.7.3", {"position": v(-35.56, -0.13) * mm});
            skPoint(sketch, "E27.7.4", {"position": v(-35.35, 3.85) * mm});
            skLineSegment(sketch, "E27.7.5", {"start": v(-37.84, -0.01) * mm, "end": v(-36.04, -0.1) * mm});
            skPoint(sketch, "E27.7.6", {"position": v(-40.54, 2.81) * mm});
            skLineSegment(sketch, "E27.7.7", {"start": v(-37.63, 3.97) * mm, "end": v(-35.83, 3.87) * mm});
            skArc(sketch, "E27.7.8", {"start": v(-38.17, 3.9) * mm, "mid": v(-39.27, 3.5) * mm, "end": v(-40.3, 2.96) * mm});
            skPoint(sketch, "E27.7.9", {"position": v(-37.9, 3.98) * mm});
            skArc(sketch, "E27.7.10", {"start": v(-35.55, -0.6) * mm, "mid": v(-35.7, -0.26) * mm, "end": v(-36.04, -0.1) * mm});
            skArc(sketch, "E27.7.11", {"start": v(-35.83, 3.87) * mm, "mid": v(-35.47, 4) * mm, "end": v(-35.3, 4.32) * mm});
            skArc(sketch, "E27.7.12", {"start": v(-37.63, 3.97) * mm, "mid": v(-37.9, 3.96) * mm, "end": v(-38.17, 3.9) * mm});
            skArc(sketch, "E27.7.13", {"start": v(-40.6, 1.7) * mm, "mid": v(-40.55, 1.46) * mm, "end": v(-40.4, 1.27) * mm});
            skArc(sketch, "E27.7.14", {"start": v(-40.3, 2.96) * mm, "mid": v(-40.48, 2.78) * mm, "end": v(-40.56, 2.55) * mm});
            skArc(sketch, "E27.7.15", {"start": v(-38.37, 0.1) * mm, "mid": v(-38.1, 0.02) * mm, "end": v(-37.84, -0.01) * mm});
            skLineSegment(sketch, "E27.7.16", {"start": v(-40.6, 1.7) * mm, "end": v(-40.58, 2.13) * mm});
            skLineSegment(sketch, "E27.7.17", {"start": v(-40.56, 2.55) * mm, "end": v(-40.58, 2.13) * mm});
            skPoint(sketch, "E27.8.0", {"position": v(-40.03, -7.04) * mm});
            skPoint(sketch, "E27.8.1", {"position": v(-37.27, -7.92) * mm});
            skArc(sketch, "E27.8.2", {"start": v(-37.55, -7.87) * mm, "mid": v(-38.69, -7.58) * mm, "end": v(-39.78, -7.16) * mm});
            skPoint(sketch, "E27.8.3", {"position": v(-34.76, -7.52) * mm});
            skPoint(sketch, "E27.8.4", {"position": v(-35.38, -3.58) * mm});
            skLineSegment(sketch, "E27.8.5", {"start": v(-37, -7.88) * mm, "end": v(-35.23, -7.6) * mm});
            skPoint(sketch, "E27.8.6", {"position": v(-40.24, -5.68) * mm});
            skLineSegment(sketch, "E27.8.7", {"start": v(-37.63, -3.94) * mm, "end": v(-35.85, -3.66) * mm});
            skArc(sketch, "E27.8.8", {"start": v(-38.15, -4.12) * mm, "mid": v(-39.14, -4.74) * mm, "end": v(-40.04, -5.49) * mm});
            skPoint(sketch, "E27.8.9", {"position": v(-37.9, -3.98) * mm});
            skArc(sketch, "E27.8.10", {"start": v(-34.65, -7.99) * mm, "mid": v(-34.86, -7.68) * mm, "end": v(-35.23, -7.6) * mm});
            skArc(sketch, "E27.8.11", {"start": v(-35.85, -3.66) * mm, "mid": v(-35.53, -3.47) * mm, "end": v(-35.42, -3.11) * mm});
            skArc(sketch, "E27.8.12", {"start": v(-37.63, -3.94) * mm, "mid": v(-37.9, -4) * mm, "end": v(-38.15, -4.12) * mm});
            skArc(sketch, "E27.8.13", {"start": v(-40.07, -6.77) * mm, "mid": v(-39.97, -7) * mm, "end": v(-39.78, -7.16) * mm});
            skArc(sketch, "E27.8.14", {"start": v(-40.04, -5.49) * mm, "mid": v(-40.18, -5.7) * mm, "end": v(-40.2, -5.94) * mm});
            skArc(sketch, "E27.8.15", {"start": v(-37.55, -7.87) * mm, "mid": v(-37.28, -7.9) * mm, "end": v(-37, -7.88) * mm});
            skLineSegment(sketch, "E27.8.16", {"start": v(-40.07, -6.77) * mm, "end": v(-40.13, -6.36) * mm});
            skLineSegment(sketch, "E27.8.17", {"start": v(-40.2, -5.94) * mm, "end": v(-40.13, -6.36) * mm});
            skPoint(sketch, "E27.9.0", {"position": v(-37.69, -15.2) * mm});
            skPoint(sketch, "E27.9.1", {"position": v(-34.8, -15.5) * mm});
            skArc(sketch, "E27.9.2", {"start": v(-35.1, -15.5) * mm, "mid": v(-36.27, -15.46) * mm, "end": v(-37.42, -15.27) * mm});
            skPoint(sketch, "E27.9.3", {"position": v(-32.43, -14.59) * mm});
            skPoint(sketch, "E27.9.4", {"position": v(-33.86, -10.86) * mm});
            skLineSegment(sketch, "E27.9.5", {"start": v(-34.56, -15.4) * mm, "end": v(-32.88, -14.76) * mm});
            skPoint(sketch, "E27.9.6", {"position": v(-38.18, -13.92) * mm});
            skLineSegment(sketch, "E27.9.7", {"start": v(-35.99, -11.68) * mm, "end": v(-34.3, -11.03) * mm});
            skArc(sketch, "E27.9.8", {"start": v(-36.46, -11.96) * mm, "mid": v(-37.3, -12.78) * mm, "end": v(-38.03, -13.7) * mm});
            skPoint(sketch, "E27.9.9", {"position": v(-36.24, -11.77) * mm});
            skArc(sketch, "E27.9.10", {"start": v(-32.23, -15.02) * mm, "mid": v(-32.5, -14.76) * mm, "end": v(-32.88, -14.76) * mm});
            skArc(sketch, "E27.9.11", {"start": v(-34.3, -11.03) * mm, "mid": v(-34.03, -10.78) * mm, "end": v(-34, -10.4) * mm});
            skArc(sketch, "E27.9.12", {"start": v(-35.99, -11.68) * mm, "mid": v(-36.24, -11.8) * mm, "end": v(-36.46, -11.96) * mm});
            skArc(sketch, "E27.9.13", {"start": v(-37.78, -14.96) * mm, "mid": v(-37.64, -15.16) * mm, "end": v(-37.42, -15.27) * mm});
            skArc(sketch, "E27.9.14", {"start": v(-38.03, -13.7) * mm, "mid": v(-38.12, -13.92) * mm, "end": v(-38.09, -14.17) * mm});
            skArc(sketch, "E27.9.15", {"start": v(-35.1, -15.5) * mm, "mid": v(-34.82, -15.48) * mm, "end": v(-34.56, -15.4) * mm});
            skLineSegment(sketch, "E27.9.16", {"start": v(-37.78, -14.96) * mm, "end": v(-37.94, -14.56) * mm});
            skLineSegment(sketch, "E27.9.17", {"start": v(-38.09, -14.17) * mm, "end": v(-37.94, -14.56) * mm});
            skPoint(sketch, "E27.10.0", {"position": v(-33.7, -22.7) * mm});
            skPoint(sketch, "E27.10.1", {"position": v(-30.82, -22.4) * mm});
            skArc(sketch, "E27.10.2", {"start": v(-31.1, -22.46) * mm, "mid": v(-32.26, -22.66) * mm, "end": v(-33.43, -22.72) * mm});
            skPoint(sketch, "E27.10.3", {"position": v(-28.7, -21) * mm});
            skPoint(sketch, "E27.10.4", {"position": v(-30.86, -17.66) * mm});
            skLineSegment(sketch, "E27.10.5", {"start": v(-30.6, -22.25) * mm, "end": v(-29.1, -21.27) * mm});
            skPoint(sketch, "E27.10.6", {"position": v(-34.45, -21.55) * mm});
            skLineSegment(sketch, "E27.10.7", {"start": v(-32.77, -18.9) * mm, "end": v(-31.26, -17.92) * mm});
            skArc(sketch, "E27.10.8", {"start": v(-33.17, -19.28) * mm, "mid": v(-33.82, -20.25) * mm, "end": v(-34.35, -21.3) * mm});
            skPoint(sketch, "E27.10.9", {"position": v(-33, -19.05) * mm});
            skArc(sketch, "E27.10.10", {"start": v(-28.4, -21.39) * mm, "mid": v(-28.73, -21.2) * mm, "end": v(-29.1, -21.27) * mm});
            skArc(sketch, "E27.10.11", {"start": v(-31.26, -17.92) * mm, "mid": v(-31.05, -17.62) * mm, "end": v(-31.1, -17.25) * mm});
            skArc(sketch, "E27.10.12", {"start": v(-32.77, -18.9) * mm, "mid": v(-33, -19.07) * mm, "end": v(-33.17, -19.28) * mm});
            skArc(sketch, "E27.10.13", {"start": v(-33.85, -22.49) * mm, "mid": v(-33.67, -22.65) * mm, "end": v(-33.43, -22.72) * mm});
            skArc(sketch, "E27.10.14", {"start": v(-34.35, -21.3) * mm, "mid": v(-34.39, -21.54) * mm, "end": v(-34.3, -21.78) * mm});
            skArc(sketch, "E27.10.15", {"start": v(-31.1, -22.46) * mm, "mid": v(-30.84, -22.38) * mm, "end": v(-30.6, -22.25) * mm});
            skLineSegment(sketch, "E27.10.16", {"start": v(-33.85, -22.49) * mm, "end": v(-34.08, -22.13) * mm});
            skLineSegment(sketch, "E27.10.17", {"start": v(-34.3, -21.78) * mm, "end": v(-34.08, -22.13) * mm});
            skPoint(sketch, "E27.11.0", {"position": v(-28.25, -29.22) * mm});
            skPoint(sketch, "E27.11.1", {"position": v(-25.5, -28.31) * mm});
            skArc(sketch, "E27.11.2", {"start": v(-25.75, -28.44) * mm, "mid": v(-26.84, -28.87) * mm, "end": v(-27.98, -29.17) * mm});
            skPoint(sketch, "E27.11.3", {"position": v(-23.7, -26.52) * mm});
            skPoint(sketch, "E27.11.4", {"position": v(-26.52, -23.7) * mm});
            skLineSegment(sketch, "E27.11.5", {"start": v(-25.3, -28.13) * mm, "end": v(-24.03, -26.85) * mm});
            skPoint(sketch, "E27.11.6", {"position": v(-29.22, -28.25) * mm});
            skLineSegment(sketch, "E27.11.7", {"start": v(-28.13, -25.3) * mm, "end": v(-26.85, -24.03) * mm});
            skArc(sketch, "E27.11.8", {"start": v(-28.44, -25.75) * mm, "mid": v(-28.87, -26.84) * mm, "end": v(-29.17, -27.98) * mm});
            skPoint(sketch, "E27.11.9", {"position": v(-28.31, -25.5) * mm});
            skArc(sketch, "E27.11.10", {"start": v(-23.34, -26.83) * mm, "mid": v(-23.7, -26.7) * mm, "end": v(-24.03, -26.85) * mm});
            skArc(sketch, "E27.11.11", {"start": v(-26.85, -24.03) * mm, "mid": v(-26.7, -23.7) * mm, "end": v(-26.83, -23.34) * mm});
            skArc(sketch, "E27.11.12", {"start": v(-28.13, -25.3) * mm, "mid": v(-28.3, -25.52) * mm, "end": v(-28.44, -25.75) * mm});
            skArc(sketch, "E27.11.13", {"start": v(-28.43, -29.03) * mm, "mid": v(-28.22, -29.16) * mm, "end": v(-27.98, -29.17) * mm});
            skArc(sketch, "E27.11.14", {"start": v(-29.17, -27.98) * mm, "mid": v(-29.16, -28.22) * mm, "end": v(-29.03, -28.43) * mm});
            skArc(sketch, "E27.11.15", {"start": v(-25.75, -28.44) * mm, "mid": v(-25.52, -28.3) * mm, "end": v(-25.3, -28.13) * mm});
            skLineSegment(sketch, "E27.11.16", {"start": v(-28.43, -29.03) * mm, "end": v(-28.73, -28.73) * mm});
            skLineSegment(sketch, "E27.11.17", {"start": v(-29.03, -28.43) * mm, "end": v(-28.73, -28.73) * mm});
            skPoint(sketch, "E27.12.0", {"position": v(-21.55, -34.45) * mm});
            skPoint(sketch, "E27.12.1", {"position": v(-19.05, -33) * mm});
            skArc(sketch, "E27.12.2", {"start": v(-19.28, -33.17) * mm, "mid": v(-20.25, -33.82) * mm, "end": v(-21.3, -34.35) * mm});
            skPoint(sketch, "E27.12.3", {"position": v(-17.66, -30.86) * mm});
            skPoint(sketch, "E27.12.4", {"position": v(-21, -28.7) * mm});
            skLineSegment(sketch, "E27.12.5", {"start": v(-18.9, -32.77) * mm, "end": v(-17.92, -31.26) * mm});
            skPoint(sketch, "E27.12.6", {"position": v(-22.7, -33.7) * mm});
            skLineSegment(sketch, "E27.12.7", {"start": v(-22.25, -30.6) * mm, "end": v(-21.27, -29.1) * mm});
            skArc(sketch, "E27.12.8", {"start": v(-22.46, -31.1) * mm, "mid": v(-22.66, -32.26) * mm, "end": v(-22.72, -33.43) * mm});
            skPoint(sketch, "E27.12.9", {"position": v(-22.4, -30.82) * mm});
            skArc(sketch, "E27.12.10", {"start": v(-17.25, -31.1) * mm, "mid": v(-17.62, -31.05) * mm, "end": v(-17.92, -31.26) * mm});
            skArc(sketch, "E27.12.11", {"start": v(-21.27, -29.1) * mm, "mid": v(-21.2, -28.73) * mm, "end": v(-21.39, -28.4) * mm});
            skArc(sketch, "E27.12.12", {"start": v(-22.25, -30.6) * mm, "mid": v(-22.38, -30.84) * mm, "end": v(-22.46, -31.1) * mm});
            skArc(sketch, "E27.12.13", {"start": v(-21.78, -34.3) * mm, "mid": v(-21.54, -34.39) * mm, "end": v(-21.3, -34.35) * mm});
            skArc(sketch, "E27.12.14", {"start": v(-22.72, -33.43) * mm, "mid": v(-22.65, -33.67) * mm, "end": v(-22.49, -33.85) * mm});
            skArc(sketch, "E27.12.15", {"start": v(-19.28, -33.17) * mm, "mid": v(-19.07, -33) * mm, "end": v(-18.9, -32.77) * mm});
            skLineSegment(sketch, "E27.12.16", {"start": v(-21.78, -34.3) * mm, "end": v(-22.13, -34.08) * mm});
            skLineSegment(sketch, "E27.12.17", {"start": v(-22.49, -33.85) * mm, "end": v(-22.13, -34.08) * mm});
            skPoint(sketch, "E27.13.0", {"position": v(-13.92, -38.18) * mm});
            skPoint(sketch, "E27.13.1", {"position": v(-11.77, -36.24) * mm});
            skArc(sketch, "E27.13.2", {"start": v(-11.96, -36.46) * mm, "mid": v(-12.78, -37.3) * mm, "end": v(-13.7, -38.03) * mm});
            skPoint(sketch, "E27.13.3", {"position": v(-10.86, -33.86) * mm});
            skPoint(sketch, "E27.13.4", {"position": v(-14.59, -32.43) * mm});
            skLineSegment(sketch, "E27.13.5", {"start": v(-11.68, -35.99) * mm, "end": v(-11.03, -34.3) * mm});
            skPoint(sketch, "E27.13.6", {"position": v(-15.2, -37.69) * mm});
            skLineSegment(sketch, "E27.13.7", {"start": v(-15.4, -34.56) * mm, "end": v(-14.76, -32.88) * mm});
            skArc(sketch, "E27.13.8", {"start": v(-15.5, -35.1) * mm, "mid": v(-15.46, -36.27) * mm, "end": v(-15.27, -37.42) * mm});
            skPoint(sketch, "E27.13.9", {"position": v(-15.5, -34.8) * mm});
            skArc(sketch, "E27.13.10", {"start": v(-10.4, -34) * mm, "mid": v(-10.78, -34.03) * mm, "end": v(-11.03, -34.3) * mm});
            skArc(sketch, "E27.13.11", {"start": v(-14.76, -32.88) * mm, "mid": v(-14.76, -32.5) * mm, "end": v(-15.02, -32.23) * mm});
            skArc(sketch, "E27.13.12", {"start": v(-15.4, -34.56) * mm, "mid": v(-15.48, -34.82) * mm, "end": v(-15.5, -35.1) * mm});
            skArc(sketch, "E27.13.13", {"start": v(-14.17, -38.09) * mm, "mid": v(-13.92, -38.12) * mm, "end": v(-13.7, -38.03) * mm});
            skArc(sketch, "E27.13.14", {"start": v(-15.27, -37.42) * mm, "mid": v(-15.16, -37.64) * mm, "end": v(-14.96, -37.78) * mm});
            skArc(sketch, "E27.13.15", {"start": v(-11.96, -36.46) * mm, "mid": v(-11.8, -36.24) * mm, "end": v(-11.68, -35.99) * mm});
            skLineSegment(sketch, "E27.13.16", {"start": v(-14.17, -38.09) * mm, "end": v(-14.56, -37.94) * mm});
            skLineSegment(sketch, "E27.13.17", {"start": v(-14.96, -37.78) * mm, "end": v(-14.56, -37.94) * mm});
            skPoint(sketch, "E27.14.0", {"position": v(-5.68, -40.24) * mm});
            skPoint(sketch, "E27.14.1", {"position": v(-3.98, -37.9) * mm});
            skArc(sketch, "E27.14.2", {"start": v(-4.12, -38.15) * mm, "mid": v(-4.74, -39.14) * mm, "end": v(-5.49, -40.04) * mm});
            skPoint(sketch, "E27.14.3", {"position": v(-3.58, -35.38) * mm});
            skPoint(sketch, "E27.14.4", {"position": v(-7.52, -34.76) * mm});
            skLineSegment(sketch, "E27.14.5", {"start": v(-3.94, -37.63) * mm, "end": v(-3.66, -35.85) * mm});
            skPoint(sketch, "E27.14.6", {"position": v(-7.04, -40.03) * mm});
            skLineSegment(sketch, "E27.14.7", {"start": v(-7.88, -37) * mm, "end": v(-7.6, -35.23) * mm});
            skArc(sketch, "E27.14.8", {"start": v(-7.87, -37.55) * mm, "mid": v(-7.58, -38.69) * mm, "end": v(-7.16, -39.78) * mm});
            skPoint(sketch, "E27.14.9", {"position": v(-7.92, -37.27) * mm});
            skArc(sketch, "E27.14.10", {"start": v(-3.11, -35.42) * mm, "mid": v(-3.47, -35.53) * mm, "end": v(-3.66, -35.85) * mm});
            skArc(sketch, "E27.14.11", {"start": v(-7.6, -35.23) * mm, "mid": v(-7.68, -34.86) * mm, "end": v(-7.99, -34.65) * mm});
            skArc(sketch, "E27.14.12", {"start": v(-7.88, -37) * mm, "mid": v(-7.9, -37.28) * mm, "end": v(-7.87, -37.55) * mm});
            skArc(sketch, "E27.14.13", {"start": v(-5.94, -40.2) * mm, "mid": v(-5.7, -40.18) * mm, "end": v(-5.49, -40.04) * mm});
            skArc(sketch, "E27.14.14", {"start": v(-7.16, -39.78) * mm, "mid": v(-7, -39.97) * mm, "end": v(-6.77, -40.07) * mm});
            skArc(sketch, "E27.14.15", {"start": v(-4.12, -38.15) * mm, "mid": v(-4, -37.9) * mm, "end": v(-3.94, -37.63) * mm});
            skLineSegment(sketch, "E27.14.16", {"start": v(-5.94, -40.2) * mm, "end": v(-6.36, -40.13) * mm});
            skLineSegment(sketch, "E27.14.17", {"start": v(-6.77, -40.07) * mm, "end": v(-6.36, -40.13) * mm});
            skPoint(sketch, "E27.15.0", {"position": v(2.81, -40.54) * mm});
            skPoint(sketch, "E27.15.1", {"position": v(3.98, -37.9) * mm});
            skArc(sketch, "E27.15.2", {"start": v(3.9, -38.17) * mm, "mid": v(3.5, -39.27) * mm, "end": v(2.96, -40.3) * mm});
            skPoint(sketch, "E27.15.3", {"position": v(3.85, -35.35) * mm});
            skPoint(sketch, "E27.15.4", {"position": v(-0.13, -35.56) * mm});
            skLineSegment(sketch, "E27.15.5", {"start": v(3.97, -37.63) * mm, "end": v(3.87, -35.83) * mm});
            skPoint(sketch, "E27.15.6", {"position": v(1.44, -40.61) * mm});
            skLineSegment(sketch, "E27.15.7", {"start": v(-0.01, -37.84) * mm, "end": v(-0.1, -36.04) * mm});
            skArc(sketch, "E27.15.8", {"start": v(0.1, -38.37) * mm, "mid": v(0.63, -39.42) * mm, "end": v(1.27, -40.4) * mm});
            skPoint(sketch, "E27.15.9", {"position": v(0, -38.1) * mm});
            skArc(sketch, "E27.15.10", {"start": v(4.32, -35.3) * mm, "mid": v(4, -35.47) * mm, "end": v(3.87, -35.83) * mm});
            skArc(sketch, "E27.15.11", {"start": v(-0.1, -36.04) * mm, "mid": v(-0.26, -35.7) * mm, "end": v(-0.6, -35.55) * mm});
            skArc(sketch, "E27.15.12", {"start": v(-0.01, -37.84) * mm, "mid": v(0.02, -38.1) * mm, "end": v(0.1, -38.37) * mm});
            skArc(sketch, "E27.15.13", {"start": v(2.55, -40.56) * mm, "mid": v(2.78, -40.48) * mm, "end": v(2.96, -40.3) * mm});
            skArc(sketch, "E27.15.14", {"start": v(1.27, -40.4) * mm, "mid": v(1.46, -40.55) * mm, "end": v(1.7, -40.6) * mm});
            skArc(sketch, "E27.15.15", {"start": v(3.9, -38.17) * mm, "mid": v(3.96, -37.9) * mm, "end": v(3.97, -37.63) * mm});
            skLineSegment(sketch, "E27.15.16", {"start": v(2.55, -40.56) * mm, "end": v(2.13, -40.58) * mm});
            skLineSegment(sketch, "E27.15.17", {"start": v(1.7, -40.6) * mm, "end": v(2.13, -40.58) * mm});
            skPoint(sketch, "E27.16.0", {"position": v(11.18, -39.07) * mm});
            skPoint(sketch, "E27.16.1", {"position": v(11.77, -36.24) * mm});
            skArc(sketch, "E27.16.2", {"start": v(11.75, -36.52) * mm, "mid": v(11.58, -37.68) * mm, "end": v(11.27, -38.81) * mm});
            skPoint(sketch, "E27.16.3", {"position": v(11.12, -33.78) * mm});
            skPoint(sketch, "E27.16.4", {"position": v(7.26, -34.81) * mm});
            skLineSegment(sketch, "E27.16.5", {"start": v(11.7, -35.98) * mm, "end": v(11.24, -34.24) * mm});
            skPoint(sketch, "E27.16.6", {"position": v(9.85, -39.43) * mm});
            skLineSegment(sketch, "E27.16.7", {"start": v(7.85, -37.01) * mm, "end": v(7.39, -35.27) * mm});
            skArc(sketch, "E27.16.8", {"start": v(8.08, -37.5) * mm, "mid": v(8.8, -38.43) * mm, "end": v(9.64, -39.25) * mm});
            skPoint(sketch, "E27.16.9", {"position": v(7.92, -37.27) * mm});
            skArc(sketch, "E27.16.10", {"start": v(11.56, -33.63) * mm, "mid": v(11.28, -33.87) * mm, "end": v(11.24, -34.24) * mm});
            skArc(sketch, "E27.16.11", {"start": v(7.39, -35.27) * mm, "mid": v(7.16, -34.97) * mm, "end": v(6.8, -34.9) * mm});
            skArc(sketch, "E27.16.12", {"start": v(7.85, -37.01) * mm, "mid": v(7.95, -37.27) * mm, "end": v(8.08, -37.5) * mm});
            skArc(sketch, "E27.16.13", {"start": v(10.92, -39.14) * mm, "mid": v(11.14, -39.02) * mm, "end": v(11.27, -38.81) * mm});
            skArc(sketch, "E27.16.14", {"start": v(9.64, -39.25) * mm, "mid": v(9.86, -39.36) * mm, "end": v(10.1, -39.36) * mm});
            skArc(sketch, "E27.16.15", {"start": v(11.75, -36.52) * mm, "mid": v(11.75, -36.25) * mm, "end": v(11.7, -35.98) * mm});
            skLineSegment(sketch, "E27.16.16", {"start": v(10.92, -39.14) * mm, "end": v(10.52, -39.25) * mm});
            skLineSegment(sketch, "E27.16.17", {"start": v(10.1, -39.36) * mm, "end": v(10.52, -39.25) * mm});
            skPoint(sketch, "E27.17.0", {"position": v(19.06, -35.9) * mm});
            skPoint(sketch, "E27.17.1", {"position": v(19.05, -33) * mm});
            skArc(sketch, "E27.17.2", {"start": v(19.1, -33.28) * mm, "mid": v(19.17, -34.45) * mm, "end": v(19.1, -35.62) * mm});
            skPoint(sketch, "E27.17.3", {"position": v(17.9, -30.73) * mm});
            skPoint(sketch, "E27.17.4", {"position": v(14.34, -32.54) * mm});
            skLineSegment(sketch, "E27.17.5", {"start": v(18.93, -32.76) * mm, "end": v(18.11, -31.15) * mm});
            skPoint(sketch, "E27.17.6", {"position": v(17.83, -36.52) * mm});
            skLineSegment(sketch, "E27.17.7", {"start": v(15.38, -34.57) * mm, "end": v(14.56, -32.96) * mm});
            skArc(sketch, "E27.17.8", {"start": v(15.7, -35) * mm, "mid": v(16.6, -35.76) * mm, "end": v(17.6, -36.39) * mm});
            skPoint(sketch, "E27.17.9", {"position": v(15.5, -34.8) * mm});
            skArc(sketch, "E27.17.10", {"start": v(18.3, -30.49) * mm, "mid": v(18.08, -30.78) * mm, "end": v(18.11, -31.15) * mm});
            skArc(sketch, "E27.17.11", {"start": v(14.56, -32.96) * mm, "mid": v(14.28, -32.72) * mm, "end": v(13.9, -32.73) * mm});
            skArc(sketch, "E27.17.12", {"start": v(15.38, -34.57) * mm, "mid": v(15.52, -34.8) * mm, "end": v(15.7, -35) * mm});
            skArc(sketch, "E27.17.13", {"start": v(18.82, -36.01) * mm, "mid": v(19, -35.85) * mm, "end": v(19.1, -35.62) * mm});
            skArc(sketch, "E27.17.14", {"start": v(17.6, -36.39) * mm, "mid": v(17.83, -36.45) * mm, "end": v(18.07, -36.4) * mm});
            skArc(sketch, "E27.17.15", {"start": v(19.1, -33.28) * mm, "mid": v(19.03, -33.01) * mm, "end": v(18.93, -32.76) * mm});
            skLineSegment(sketch, "E27.17.16", {"start": v(18.82, -36.01) * mm, "end": v(18.45, -36.2) * mm});
            skLineSegment(sketch, "E27.17.17", {"start": v(18.07, -36.4) * mm, "end": v(18.45, -36.2) * mm});
            skPoint(sketch, "E27.18.0", {"position": v(26.1, -31.15) * mm});
            skPoint(sketch, "E27.18.1", {"position": v(25.5, -28.31) * mm});
            skArc(sketch, "E27.18.2", {"start": v(25.6, -28.59) * mm, "mid": v(25.91, -29.71) * mm, "end": v(26.09, -30.87) * mm});
            skPoint(sketch, "E27.18.3", {"position": v(23.9, -26.34) * mm});
            skPoint(sketch, "E27.18.4", {"position": v(20.8, -28.85) * mm});
            skLineSegment(sketch, "E27.18.5", {"start": v(25.33, -28.1) * mm, "end": v(24.2, -26.7) * mm});
            skPoint(sketch, "E27.18.6", {"position": v(25.04, -32.01) * mm});
            skLineSegment(sketch, "E27.18.7", {"start": v(22.23, -30.62) * mm, "end": v(21.1, -29.22) * mm});
            skArc(sketch, "E27.18.8", {"start": v(22.64, -30.98) * mm, "mid": v(23.68, -31.52) * mm, "end": v(24.77, -31.94) * mm});
            skPoint(sketch, "E27.18.9", {"position": v(22.4, -30.82) * mm});
            skArc(sketch, "E27.18.10", {"start": v(24.24, -26.02) * mm, "mid": v(24.08, -26.35) * mm, "end": v(24.2, -26.7) * mm});
            skArc(sketch, "E27.18.11", {"start": v(21.1, -29.22) * mm, "mid": v(20.77, -29.03) * mm, "end": v(20.4, -29.12) * mm});
            skArc(sketch, "E27.18.12", {"start": v(22.23, -30.62) * mm, "mid": v(22.42, -30.82) * mm, "end": v(22.64, -30.98) * mm});
            skArc(sketch, "E27.18.13", {"start": v(25.9, -31.31) * mm, "mid": v(26.05, -31.12) * mm, "end": v(26.09, -30.87) * mm});
            skArc(sketch, "E27.18.14", {"start": v(24.77, -31.94) * mm, "mid": v(25.02, -31.95) * mm, "end": v(25.24, -31.84) * mm});
            skArc(sketch, "E27.18.15", {"start": v(25.6, -28.59) * mm, "mid": v(25.48, -28.34) * mm, "end": v(25.33, -28.1) * mm});
            skLineSegment(sketch, "E27.18.16", {"start": v(25.9, -31.31) * mm, "end": v(25.57, -31.58) * mm});
            skLineSegment(sketch, "E27.18.17", {"start": v(25.24, -31.84) * mm, "end": v(25.57, -31.58) * mm});
            skPoint(sketch, "E27.19.0", {"position": v(32.01, -25.04) * mm});
            skPoint(sketch, "E27.19.1", {"position": v(30.82, -22.4) * mm});
            skArc(sketch, "E27.19.2", {"start": v(30.98, -22.64) * mm, "mid": v(31.52, -23.68) * mm, "end": v(31.94, -24.77) * mm});
            skPoint(sketch, "E27.19.3", {"position": v(28.85, -20.8) * mm});
            skPoint(sketch, "E27.19.4", {"position": v(26.34, -23.9) * mm});
            skLineSegment(sketch, "E27.19.5", {"start": v(30.62, -22.23) * mm, "end": v(29.22, -21.1) * mm});
            skPoint(sketch, "E27.19.6", {"position": v(31.15, -26.1) * mm});
            skLineSegment(sketch, "E27.19.7", {"start": v(28.1, -25.33) * mm, "end": v(26.7, -24.2) * mm});
            skArc(sketch, "E27.19.8", {"start": v(28.59, -25.6) * mm, "mid": v(29.71, -25.91) * mm, "end": v(30.87, -26.09) * mm});
            skPoint(sketch, "E27.19.9", {"position": v(28.31, -25.5) * mm});
            skArc(sketch, "E27.19.10", {"start": v(29.12, -20.4) * mm, "mid": v(29.03, -20.77) * mm, "end": v(29.22, -21.1) * mm});
            skArc(sketch, "E27.19.11", {"start": v(26.7, -24.2) * mm, "mid": v(26.35, -24.08) * mm, "end": v(26.02, -24.24) * mm});
            skArc(sketch, "E27.19.12", {"start": v(28.1, -25.33) * mm, "mid": v(28.34, -25.48) * mm, "end": v(28.59, -25.6) * mm});
            skArc(sketch, "E27.19.13", {"start": v(31.84, -25.24) * mm, "mid": v(31.95, -25.02) * mm, "end": v(31.94, -24.77) * mm});
            skArc(sketch, "E27.19.14", {"start": v(30.87, -26.09) * mm, "mid": v(31.12, -26.05) * mm, "end": v(31.31, -25.9) * mm});
            skArc(sketch, "E27.19.15", {"start": v(30.98, -22.64) * mm, "mid": v(30.82, -22.42) * mm, "end": v(30.62, -22.23) * mm});
            skLineSegment(sketch, "E27.19.16", {"start": v(31.84, -25.24) * mm, "end": v(31.58, -25.57) * mm});
            skLineSegment(sketch, "E27.19.17", {"start": v(31.31, -25.9) * mm, "end": v(31.58, -25.57) * mm});
            skPoint(sketch, "E27.20.0", {"position": v(36.52, -17.83) * mm});
            skPoint(sketch, "E27.20.1", {"position": v(34.8, -15.5) * mm});
            skArc(sketch, "E27.20.2", {"start": v(35, -15.7) * mm, "mid": v(35.76, -16.6) * mm, "end": v(36.39, -17.6) * mm});
            skPoint(sketch, "E27.20.3", {"position": v(32.54, -14.34) * mm});
            skPoint(sketch, "E27.20.4", {"position": v(30.73, -17.9) * mm});
            skLineSegment(sketch, "E27.20.5", {"start": v(34.57, -15.38) * mm, "end": v(32.96, -14.56) * mm});
            skPoint(sketch, "E27.20.6", {"position": v(35.9, -19.06) * mm});
            skLineSegment(sketch, "E27.20.7", {"start": v(32.76, -18.93) * mm, "end": v(31.15, -18.11) * mm});
            skArc(sketch, "E27.20.8", {"start": v(33.28, -19.1) * mm, "mid": v(34.45, -19.17) * mm, "end": v(35.62, -19.1) * mm});
            skPoint(sketch, "E27.20.9", {"position": v(33, -19.05) * mm});
            skArc(sketch, "E27.20.10", {"start": v(32.73, -13.9) * mm, "mid": v(32.72, -14.28) * mm, "end": v(32.96, -14.56) * mm});
            skArc(sketch, "E27.20.11", {"start": v(31.15, -18.11) * mm, "mid": v(30.78, -18.08) * mm, "end": v(30.49, -18.3) * mm});
            skArc(sketch, "E27.20.12", {"start": v(32.76, -18.93) * mm, "mid": v(33.01, -19.03) * mm, "end": v(33.28, -19.1) * mm});
            skArc(sketch, "E27.20.13", {"start": v(36.4, -18.07) * mm, "mid": v(36.45, -17.83) * mm, "end": v(36.39, -17.6) * mm});
            skArc(sketch, "E27.20.14", {"start": v(35.62, -19.1) * mm, "mid": v(35.85, -19) * mm, "end": v(36.01, -18.82) * mm});
            skArc(sketch, "E27.20.15", {"start": v(35, -15.7) * mm, "mid": v(34.8, -15.52) * mm, "end": v(34.57, -15.38) * mm});
            skLineSegment(sketch, "E27.20.16", {"start": v(36.4, -18.07) * mm, "end": v(36.2, -18.45) * mm});
            skLineSegment(sketch, "E27.20.17", {"start": v(36.01, -18.82) * mm, "end": v(36.2, -18.45) * mm});
            skPoint(sketch, "E27.21.0", {"position": v(39.43, -9.85) * mm});
            skPoint(sketch, "E27.21.1", {"position": v(37.27, -7.92) * mm});
            skArc(sketch, "E27.21.2", {"start": v(37.5, -8.08) * mm, "mid": v(38.43, -8.8) * mm, "end": v(39.25, -9.64) * mm});
            skPoint(sketch, "E27.21.3", {"position": v(34.81, -7.26) * mm});
            skPoint(sketch, "E27.21.4", {"position": v(33.78, -11.12) * mm});
            skLineSegment(sketch, "E27.21.5", {"start": v(37.01, -7.85) * mm, "end": v(35.27, -7.39) * mm});
            skPoint(sketch, "E27.21.6", {"position": v(39.07, -11.18) * mm});
            skLineSegment(sketch, "E27.21.7", {"start": v(35.98, -11.7) * mm, "end": v(34.24, -11.24) * mm});
            skArc(sketch, "E27.21.8", {"start": v(36.52, -11.75) * mm, "mid": v(37.68, -11.58) * mm, "end": v(38.81, -11.27) * mm});
            skPoint(sketch, "E27.21.9", {"position": v(36.24, -11.77) * mm});
            skArc(sketch, "E27.21.10", {"start": v(34.9, -6.8) * mm, "mid": v(34.97, -7.16) * mm, "end": v(35.27, -7.39) * mm});
            skArc(sketch, "E27.21.11", {"start": v(34.24, -11.24) * mm, "mid": v(33.87, -11.28) * mm, "end": v(33.63, -11.56) * mm});
            skArc(sketch, "E27.21.12", {"start": v(35.98, -11.7) * mm, "mid": v(36.25, -11.75) * mm, "end": v(36.52, -11.75) * mm});
            skArc(sketch, "E27.21.13", {"start": v(39.36, -10.1) * mm, "mid": v(39.36, -9.86) * mm, "end": v(39.25, -9.64) * mm});
            skArc(sketch, "E27.21.14", {"start": v(38.81, -11.27) * mm, "mid": v(39.02, -11.14) * mm, "end": v(39.14, -10.92) * mm});
            skArc(sketch, "E27.21.15", {"start": v(37.5, -8.08) * mm, "mid": v(37.27, -7.95) * mm, "end": v(37.01, -7.85) * mm});
            skLineSegment(sketch, "E27.21.16", {"start": v(39.36, -10.1) * mm, "end": v(39.25, -10.52) * mm});
            skLineSegment(sketch, "E27.21.17", {"start": v(39.14, -10.92) * mm, "end": v(39.25, -10.52) * mm});
            skPoint(sketch, "E27.22.0", {"position": v(40.61, -1.44) * mm});
            skPoint(sketch, "E27.22.1", {"position": v(38.1, 0) * mm});
            skArc(sketch, "E27.22.2", {"start": v(38.37, -0.1) * mm, "mid": v(39.42, -0.63) * mm, "end": v(40.4, -1.27) * mm});
            skPoint(sketch, "E27.22.3", {"position": v(35.56, 0.13) * mm});
            skPoint(sketch, "E27.22.4", {"position": v(35.35, -3.85) * mm});
            skLineSegment(sketch, "E27.22.5", {"start": v(37.84, 0.01) * mm, "end": v(36.04, 0.1) * mm});
            skPoint(sketch, "E27.22.6", {"position": v(40.54, -2.81) * mm});
            skLineSegment(sketch, "E27.22.7", {"start": v(37.63, -3.97) * mm, "end": v(35.83, -3.87) * mm});
            skArc(sketch, "E27.22.8", {"start": v(38.17, -3.9) * mm, "mid": v(39.27, -3.5) * mm, "end": v(40.3, -2.96) * mm});
            skPoint(sketch, "E27.22.9", {"position": v(37.9, -3.98) * mm});
            skArc(sketch, "E27.22.10", {"start": v(35.55, 0.6) * mm, "mid": v(35.7, 0.26) * mm, "end": v(36.04, 0.1) * mm});
            skArc(sketch, "E27.22.11", {"start": v(35.83, -3.87) * mm, "mid": v(35.47, -4) * mm, "end": v(35.3, -4.32) * mm});
            skArc(sketch, "E27.22.12", {"start": v(37.63, -3.97) * mm, "mid": v(37.9, -3.96) * mm, "end": v(38.17, -3.9) * mm});
            skArc(sketch, "E27.22.13", {"start": v(40.6, -1.7) * mm, "mid": v(40.55, -1.46) * mm, "end": v(40.4, -1.27) * mm});
            skArc(sketch, "E27.22.14", {"start": v(40.3, -2.96) * mm, "mid": v(40.48, -2.78) * mm, "end": v(40.56, -2.55) * mm});
            skArc(sketch, "E27.22.15", {"start": v(38.37, -0.1) * mm, "mid": v(38.1, -0.02) * mm, "end": v(37.84, 0.01) * mm});
            skLineSegment(sketch, "E27.22.16", {"start": v(40.6, -1.7) * mm, "end": v(40.58, -2.13) * mm});
            skLineSegment(sketch, "E27.22.17", {"start": v(40.56, -2.55) * mm, "end": v(40.58, -2.13) * mm});
            skPoint(sketch, "E27.23.0", {"position": v(40.03, 7.04) * mm});
            skPoint(sketch, "E27.23.1", {"position": v(37.27, 7.92) * mm});
            skArc(sketch, "E27.23.2", {"start": v(37.55, 7.87) * mm, "mid": v(38.69, 7.58) * mm, "end": v(39.78, 7.16) * mm});
            skPoint(sketch, "E27.23.3", {"position": v(34.76, 7.52) * mm});
            skPoint(sketch, "E27.23.4", {"position": v(35.38, 3.58) * mm});
            skLineSegment(sketch, "E27.23.5", {"start": v(37, 7.88) * mm, "end": v(35.23, 7.6) * mm});
            skPoint(sketch, "E27.23.6", {"position": v(40.24, 5.68) * mm});
            skLineSegment(sketch, "E27.23.7", {"start": v(37.63, 3.94) * mm, "end": v(35.85, 3.66) * mm});
            skArc(sketch, "E27.23.8", {"start": v(38.15, 4.12) * mm, "mid": v(39.14, 4.74) * mm, "end": v(40.04, 5.49) * mm});
            skPoint(sketch, "E27.23.9", {"position": v(37.9, 3.98) * mm});
            skArc(sketch, "E27.23.10", {"start": v(34.65, 7.99) * mm, "mid": v(34.86, 7.68) * mm, "end": v(35.23, 7.6) * mm});
            skArc(sketch, "E27.23.11", {"start": v(35.85, 3.66) * mm, "mid": v(35.53, 3.47) * mm, "end": v(35.42, 3.11) * mm});
            skArc(sketch, "E27.23.12", {"start": v(37.63, 3.94) * mm, "mid": v(37.9, 4) * mm, "end": v(38.15, 4.12) * mm});
            skArc(sketch, "E27.23.13", {"start": v(40.07, 6.77) * mm, "mid": v(39.97, 7) * mm, "end": v(39.78, 7.16) * mm});
            skArc(sketch, "E27.23.14", {"start": v(40.04, 5.49) * mm, "mid": v(40.18, 5.7) * mm, "end": v(40.2, 5.94) * mm});
            skArc(sketch, "E27.23.15", {"start": v(37.55, 7.87) * mm, "mid": v(37.28, 7.9) * mm, "end": v(37, 7.88) * mm});
            skLineSegment(sketch, "E27.23.16", {"start": v(40.07, 6.77) * mm, "end": v(40.13, 6.36) * mm});
            skLineSegment(sketch, "E27.23.17", {"start": v(40.2, 5.94) * mm, "end": v(40.13, 6.36) * mm});
            skPoint(sketch, "E27.24.0", {"position": v(37.69, 15.2) * mm});
            skPoint(sketch, "E27.24.1", {"position": v(34.8, 15.5) * mm});
            skArc(sketch, "E27.24.2", {"start": v(35.1, 15.5) * mm, "mid": v(36.27, 15.46) * mm, "end": v(37.42, 15.27) * mm});
            skPoint(sketch, "E27.24.3", {"position": v(32.43, 14.59) * mm});
            skPoint(sketch, "E27.24.4", {"position": v(33.86, 10.86) * mm});
            skLineSegment(sketch, "E27.24.5", {"start": v(34.56, 15.4) * mm, "end": v(32.88, 14.76) * mm});
            skPoint(sketch, "E27.24.6", {"position": v(38.18, 13.92) * mm});
            skLineSegment(sketch, "E27.24.7", {"start": v(35.99, 11.68) * mm, "end": v(34.3, 11.03) * mm});
            skArc(sketch, "E27.24.8", {"start": v(36.46, 11.96) * mm, "mid": v(37.3, 12.78) * mm, "end": v(38.03, 13.7) * mm});
            skPoint(sketch, "E27.24.9", {"position": v(36.24, 11.77) * mm});
            skArc(sketch, "E27.24.10", {"start": v(32.23, 15.02) * mm, "mid": v(32.5, 14.76) * mm, "end": v(32.88, 14.76) * mm});
            skArc(sketch, "E27.24.11", {"start": v(34.3, 11.03) * mm, "mid": v(34.03, 10.78) * mm, "end": v(34, 10.4) * mm});
            skArc(sketch, "E27.24.12", {"start": v(35.99, 11.68) * mm, "mid": v(36.24, 11.8) * mm, "end": v(36.46, 11.96) * mm});
            skArc(sketch, "E27.24.13", {"start": v(37.78, 14.96) * mm, "mid": v(37.64, 15.16) * mm, "end": v(37.42, 15.27) * mm});
            skArc(sketch, "E27.24.14", {"start": v(38.03, 13.7) * mm, "mid": v(38.12, 13.92) * mm, "end": v(38.09, 14.17) * mm});
            skArc(sketch, "E27.24.15", {"start": v(35.1, 15.5) * mm, "mid": v(34.82, 15.48) * mm, "end": v(34.56, 15.4) * mm});
            skLineSegment(sketch, "E27.24.16", {"start": v(37.78, 14.96) * mm, "end": v(37.94, 14.56) * mm});
            skLineSegment(sketch, "E27.24.17", {"start": v(38.09, 14.17) * mm, "end": v(37.94, 14.56) * mm});
            skPoint(sketch, "E27.25.0", {"position": v(33.7, 22.7) * mm});
            skPoint(sketch, "E27.25.1", {"position": v(30.82, 22.4) * mm});
            skArc(sketch, "E27.25.2", {"start": v(31.1, 22.46) * mm, "mid": v(32.26, 22.66) * mm, "end": v(33.43, 22.72) * mm});
            skPoint(sketch, "E27.25.3", {"position": v(28.7, 21) * mm});
            skPoint(sketch, "E27.25.4", {"position": v(30.86, 17.66) * mm});
            skLineSegment(sketch, "E27.25.5", {"start": v(30.6, 22.25) * mm, "end": v(29.1, 21.27) * mm});
            skPoint(sketch, "E27.25.6", {"position": v(34.45, 21.55) * mm});
            skLineSegment(sketch, "E27.25.7", {"start": v(32.77, 18.9) * mm, "end": v(31.26, 17.92) * mm});
            skArc(sketch, "E27.25.8", {"start": v(33.17, 19.28) * mm, "mid": v(33.82, 20.25) * mm, "end": v(34.35, 21.3) * mm});
            skPoint(sketch, "E27.25.9", {"position": v(33, 19.05) * mm});
            skArc(sketch, "E27.25.10", {"start": v(28.4, 21.39) * mm, "mid": v(28.73, 21.2) * mm, "end": v(29.1, 21.27) * mm});
            skArc(sketch, "E27.25.11", {"start": v(31.26, 17.92) * mm, "mid": v(31.05, 17.62) * mm, "end": v(31.1, 17.25) * mm});
            skArc(sketch, "E27.25.12", {"start": v(32.77, 18.9) * mm, "mid": v(33, 19.07) * mm, "end": v(33.17, 19.28) * mm});
            skArc(sketch, "E27.25.13", {"start": v(33.85, 22.49) * mm, "mid": v(33.67, 22.65) * mm, "end": v(33.43, 22.72) * mm});
            skArc(sketch, "E27.25.14", {"start": v(34.35, 21.3) * mm, "mid": v(34.39, 21.54) * mm, "end": v(34.3, 21.78) * mm});
            skArc(sketch, "E27.25.15", {"start": v(31.1, 22.46) * mm, "mid": v(30.84, 22.38) * mm, "end": v(30.6, 22.25) * mm});
            skLineSegment(sketch, "E27.25.16", {"start": v(33.85, 22.49) * mm, "end": v(34.08, 22.13) * mm});
            skLineSegment(sketch, "E27.25.17", {"start": v(34.3, 21.78) * mm, "end": v(34.08, 22.13) * mm});
            skPoint(sketch, "E27.26.0", {"position": v(28.25, 29.22) * mm});
            skPoint(sketch, "E27.26.1", {"position": v(25.5, 28.31) * mm});
            skArc(sketch, "E27.26.2", {"start": v(25.75, 28.44) * mm, "mid": v(26.84, 28.87) * mm, "end": v(27.98, 29.17) * mm});
            skPoint(sketch, "E27.26.3", {"position": v(23.7, 26.52) * mm});
            skPoint(sketch, "E27.26.4", {"position": v(26.52, 23.7) * mm});
            skLineSegment(sketch, "E27.26.5", {"start": v(25.3, 28.13) * mm, "end": v(24.03, 26.85) * mm});
            skPoint(sketch, "E27.26.6", {"position": v(29.22, 28.25) * mm});
            skLineSegment(sketch, "E27.26.7", {"start": v(28.13, 25.3) * mm, "end": v(26.85, 24.03) * mm});
            skArc(sketch, "E27.26.8", {"start": v(28.44, 25.75) * mm, "mid": v(28.87, 26.84) * mm, "end": v(29.17, 27.98) * mm});
            skPoint(sketch, "E27.26.9", {"position": v(28.31, 25.5) * mm});
            skArc(sketch, "E27.26.10", {"start": v(23.34, 26.83) * mm, "mid": v(23.7, 26.7) * mm, "end": v(24.03, 26.85) * mm});
            skArc(sketch, "E27.26.11", {"start": v(26.85, 24.03) * mm, "mid": v(26.7, 23.7) * mm, "end": v(26.83, 23.34) * mm});
            skArc(sketch, "E27.26.12", {"start": v(28.13, 25.3) * mm, "mid": v(28.3, 25.52) * mm, "end": v(28.44, 25.75) * mm});
            skArc(sketch, "E27.26.13", {"start": v(28.43, 29.03) * mm, "mid": v(28.22, 29.16) * mm, "end": v(27.98, 29.17) * mm});
            skArc(sketch, "E27.26.14", {"start": v(29.17, 27.98) * mm, "mid": v(29.16, 28.22) * mm, "end": v(29.03, 28.43) * mm});
            skArc(sketch, "E27.26.15", {"start": v(25.75, 28.44) * mm, "mid": v(25.52, 28.3) * mm, "end": v(25.3, 28.13) * mm});
            skLineSegment(sketch, "E27.26.16", {"start": v(28.43, 29.03) * mm, "end": v(28.73, 28.73) * mm});
            skLineSegment(sketch, "E27.26.17", {"start": v(29.03, 28.43) * mm, "end": v(28.73, 28.73) * mm});
            skPoint(sketch, "E27.27.0", {"position": v(21.55, 34.45) * mm});
            skPoint(sketch, "E27.27.1", {"position": v(19.05, 33) * mm});
            skArc(sketch, "E27.27.2", {"start": v(19.28, 33.17) * mm, "mid": v(20.25, 33.82) * mm, "end": v(21.3, 34.35) * mm});
            skPoint(sketch, "E27.27.3", {"position": v(17.66, 30.86) * mm});
            skPoint(sketch, "E27.27.4", {"position": v(21, 28.7) * mm});
            skLineSegment(sketch, "E27.27.5", {"start": v(18.9, 32.77) * mm, "end": v(17.92, 31.26) * mm});
            skPoint(sketch, "E27.27.6", {"position": v(22.7, 33.7) * mm});
            skLineSegment(sketch, "E27.27.7", {"start": v(22.25, 30.6) * mm, "end": v(21.27, 29.1) * mm});
            skArc(sketch, "E27.27.8", {"start": v(22.46, 31.1) * mm, "mid": v(22.66, 32.26) * mm, "end": v(22.72, 33.43) * mm});
            skPoint(sketch, "E27.27.9", {"position": v(22.4, 30.82) * mm});
            skArc(sketch, "E27.27.10", {"start": v(17.25, 31.1) * mm, "mid": v(17.62, 31.05) * mm, "end": v(17.92, 31.26) * mm});
            skArc(sketch, "E27.27.11", {"start": v(21.27, 29.1) * mm, "mid": v(21.2, 28.73) * mm, "end": v(21.39, 28.4) * mm});
            skArc(sketch, "E27.27.12", {"start": v(22.25, 30.6) * mm, "mid": v(22.38, 30.84) * mm, "end": v(22.46, 31.1) * mm});
            skArc(sketch, "E27.27.13", {"start": v(21.78, 34.3) * mm, "mid": v(21.54, 34.39) * mm, "end": v(21.3, 34.35) * mm});
            skArc(sketch, "E27.27.14", {"start": v(22.72, 33.43) * mm, "mid": v(22.65, 33.67) * mm, "end": v(22.49, 33.85) * mm});
            skArc(sketch, "E27.27.15", {"start": v(19.28, 33.17) * mm, "mid": v(19.07, 33) * mm, "end": v(18.9, 32.77) * mm});
            skLineSegment(sketch, "E27.27.16", {"start": v(21.78, 34.3) * mm, "end": v(22.13, 34.08) * mm});
            skLineSegment(sketch, "E27.27.17", {"start": v(22.49, 33.85) * mm, "end": v(22.13, 34.08) * mm});
            skPoint(sketch, "E27.28.0", {"position": v(13.92, 38.18) * mm});
            skPoint(sketch, "E27.28.1", {"position": v(11.77, 36.24) * mm});
            skArc(sketch, "E27.28.2", {"start": v(11.96, 36.46) * mm, "mid": v(12.78, 37.3) * mm, "end": v(13.7, 38.03) * mm});
            skPoint(sketch, "E27.28.3", {"position": v(10.86, 33.86) * mm});
            skPoint(sketch, "E27.28.4", {"position": v(14.59, 32.43) * mm});
            skLineSegment(sketch, "E27.28.5", {"start": v(11.68, 35.99) * mm, "end": v(11.03, 34.3) * mm});
            skPoint(sketch, "E27.28.6", {"position": v(15.2, 37.69) * mm});
            skLineSegment(sketch, "E27.28.7", {"start": v(15.4, 34.56) * mm, "end": v(14.76, 32.88) * mm});
            skArc(sketch, "E27.28.8", {"start": v(15.5, 35.1) * mm, "mid": v(15.46, 36.27) * mm, "end": v(15.27, 37.42) * mm});
            skPoint(sketch, "E27.28.9", {"position": v(15.5, 34.8) * mm});
            skArc(sketch, "E27.28.10", {"start": v(10.4, 34) * mm, "mid": v(10.78, 34.03) * mm, "end": v(11.03, 34.3) * mm});
            skArc(sketch, "E27.28.11", {"start": v(14.76, 32.88) * mm, "mid": v(14.76, 32.5) * mm, "end": v(15.02, 32.23) * mm});
            skArc(sketch, "E27.28.12", {"start": v(15.4, 34.56) * mm, "mid": v(15.48, 34.82) * mm, "end": v(15.5, 35.1) * mm});
            skArc(sketch, "E27.28.13", {"start": v(14.17, 38.09) * mm, "mid": v(13.92, 38.12) * mm, "end": v(13.7, 38.03) * mm});
            skArc(sketch, "E27.28.14", {"start": v(15.27, 37.42) * mm, "mid": v(15.16, 37.64) * mm, "end": v(14.96, 37.78) * mm});
            skArc(sketch, "E27.28.15", {"start": v(11.96, 36.46) * mm, "mid": v(11.8, 36.24) * mm, "end": v(11.68, 35.99) * mm});
            skLineSegment(sketch, "E27.28.16", {"start": v(14.17, 38.09) * mm, "end": v(14.56, 37.94) * mm});
            skLineSegment(sketch, "E27.28.17", {"start": v(14.96, 37.78) * mm, "end": v(14.56, 37.94) * mm});
            skPoint(sketch, "E27.29.0", {"position": v(5.68, 40.24) * mm});
            skPoint(sketch, "E27.29.1", {"position": v(3.98, 37.9) * mm});
            skArc(sketch, "E27.29.2", {"start": v(4.12, 38.15) * mm, "mid": v(4.74, 39.14) * mm, "end": v(5.49, 40.04) * mm});
            skPoint(sketch, "E27.29.3", {"position": v(3.58, 35.38) * mm});
            skPoint(sketch, "E27.29.4", {"position": v(7.52, 34.76) * mm});
            skLineSegment(sketch, "E27.29.5", {"start": v(3.94, 37.63) * mm, "end": v(3.66, 35.85) * mm});
            skPoint(sketch, "E27.29.6", {"position": v(7.04, 40.03) * mm});
            skLineSegment(sketch, "E27.29.7", {"start": v(7.88, 37) * mm, "end": v(7.6, 35.23) * mm});
            skArc(sketch, "E27.29.8", {"start": v(7.87, 37.55) * mm, "mid": v(7.58, 38.69) * mm, "end": v(7.16, 39.78) * mm});
            skPoint(sketch, "E27.29.9", {"position": v(7.92, 37.27) * mm});
            skArc(sketch, "E27.29.10", {"start": v(3.11, 35.42) * mm, "mid": v(3.47, 35.53) * mm, "end": v(3.66, 35.85) * mm});
            skArc(sketch, "E27.29.11", {"start": v(7.6, 35.23) * mm, "mid": v(7.68, 34.86) * mm, "end": v(7.99, 34.65) * mm});
            skArc(sketch, "E27.29.12", {"start": v(7.88, 37) * mm, "mid": v(7.9, 37.28) * mm, "end": v(7.87, 37.55) * mm});
            skArc(sketch, "E27.29.13", {"start": v(5.94, 40.2) * mm, "mid": v(5.7, 40.18) * mm, "end": v(5.49, 40.04) * mm});
            skArc(sketch, "E27.29.14", {"start": v(7.16, 39.78) * mm, "mid": v(7, 39.97) * mm, "end": v(6.77, 40.07) * mm});
            skArc(sketch, "E27.29.15", {"start": v(4.12, 38.15) * mm, "mid": v(4, 37.9) * mm, "end": v(3.94, 37.63) * mm});
            skLineSegment(sketch, "E27.29.16", {"start": v(5.94, 40.2) * mm, "end": v(6.36, 40.13) * mm});
            skLineSegment(sketch, "E27.29.17", {"start": v(6.77, 40.07) * mm, "end": v(6.36, 40.13) * mm});
            skPoint(sketch, "E27.center", {"position": v(0, 0) * mm});
            skLineSegment(sketch, "E28", {"start": v(0.6, 35.55) * mm, "end": v(3.11, 35.42) * mm});
            skLineSegment(sketch, "E29.1.0", {"start": v(-6.8, 34.9) * mm, "end": v(-4.32, 35.3) * mm});
            skLineSegment(sketch, "E29.2.0", {"start": v(-13.9, 32.73) * mm, "end": v(-11.56, 33.63) * mm});
            skLineSegment(sketch, "E29.3.0", {"start": v(-20.4, 29.12) * mm, "end": v(-18.3, 30.49) * mm});
            skLineSegment(sketch, "E29.4.0", {"start": v(-26.02, 24.24) * mm, "end": v(-24.24, 26.02) * mm});
            skLineSegment(sketch, "E29.5.0", {"start": v(-30.49, 18.3) * mm, "end": v(-29.12, 20.4) * mm});
            skLineSegment(sketch, "E29.6.0", {"start": v(-33.63, 11.56) * mm, "end": v(-32.73, 13.9) * mm});
            skLineSegment(sketch, "E29.7.0", {"start": v(-35.3, 4.32) * mm, "end": v(-34.9, 6.8) * mm});
            skLineSegment(sketch, "E29.8.0", {"start": v(-35.42, -3.11) * mm, "end": v(-35.55, -0.6) * mm});
            skLineSegment(sketch, "E29.9.0", {"start": v(-34, -10.4) * mm, "end": v(-34.65, -7.99) * mm});
            skLineSegment(sketch, "E29.10.0", {"start": v(-31.1, -17.25) * mm, "end": v(-32.23, -15.02) * mm});
            skLineSegment(sketch, "E29.11.0", {"start": v(-26.83, -23.34) * mm, "end": v(-28.4, -21.39) * mm});
            skLineSegment(sketch, "E29.12.0", {"start": v(-21.39, -28.4) * mm, "end": v(-23.34, -26.83) * mm});
            skLineSegment(sketch, "E29.13.0", {"start": v(-15.02, -32.23) * mm, "end": v(-17.25, -31.1) * mm});
            skLineSegment(sketch, "E29.14.0", {"start": v(-7.99, -34.65) * mm, "end": v(-10.4, -34) * mm});
            skLineSegment(sketch, "E29.15.0", {"start": v(-0.6, -35.55) * mm, "end": v(-3.11, -35.42) * mm});
            skLineSegment(sketch, "E29.16.0", {"start": v(6.8, -34.9) * mm, "end": v(4.32, -35.3) * mm});
            skLineSegment(sketch, "E29.17.0", {"start": v(13.9, -32.73) * mm, "end": v(11.56, -33.63) * mm});
            skLineSegment(sketch, "E29.18.0", {"start": v(20.4, -29.12) * mm, "end": v(18.3, -30.49) * mm});
            skLineSegment(sketch, "E29.19.0", {"start": v(26.02, -24.24) * mm, "end": v(24.24, -26.02) * mm});
            skLineSegment(sketch, "E29.20.0", {"start": v(30.49, -18.3) * mm, "end": v(29.12, -20.4) * mm});
            skLineSegment(sketch, "E29.21.0", {"start": v(33.63, -11.56) * mm, "end": v(32.73, -13.9) * mm});
            skLineSegment(sketch, "E29.22.0", {"start": v(35.3, -4.32) * mm, "end": v(34.9, -6.8) * mm});
            skLineSegment(sketch, "E29.23.0", {"start": v(35.42, 3.11) * mm, "end": v(35.55, 0.6) * mm});
            skLineSegment(sketch, "E29.24.0", {"start": v(34, 10.4) * mm, "end": v(34.65, 7.99) * mm});
            skLineSegment(sketch, "E29.25.0", {"start": v(31.1, 17.25) * mm, "end": v(32.23, 15.02) * mm});
            skLineSegment(sketch, "E29.26.0", {"start": v(26.83, 23.34) * mm, "end": v(28.4, 21.39) * mm});
            skLineSegment(sketch, "E29.27.0", {"start": v(21.39, 28.4) * mm, "end": v(23.34, 26.83) * mm});
            skLineSegment(sketch, "E29.28.0", {"start": v(15.02, 32.23) * mm, "end": v(17.25, 31.1) * mm});
            skLineSegment(sketch, "E29.29.0", {"start": v(7.99, 34.65) * mm, "end": v(10.4, 34) * mm});
            skSolve(sketch);
        }
        {
            var Q0;
            Q0=makeQuery(id+"F0.imprint","IMPRINT",FACE,{"disambiguationData":[TD([[makeQuery(id+"F0.imprint","IMPRINT",EDGE,{"derivedFrom":sQuery(id+"F0.wireOp",EDGE,"E0")}),1.0]])]});
            var Q1;
            Q1=makeQuery(id+"F2.imprint","IMPRINT",FACE,{"disambiguationData":[TD([[makeQuery(id+"F2.imprint","IMPRINT",EDGE,{"derivedFrom":sQuery(id+"F2.wireOp",EDGE,"E15")}),1.0]])]});
            var Q2;
            Q2=sQuery(id+"F0.wireOp",VERTEX,"E2.end");
            var Q3;
            Q3=sQuery(id+"F2.wireOp",VERTEX,"E27.29.11.start");
            loft(context, id + "F3", {"sheetProfilesArray" : [{ "sheetProfileEntities" : qUnion([Q0]) }, { "sheetProfileEntities" : qUnion([Q1]) }], "matchConnections" : true, "connections" : [{ "connectionEntities" : qUnion([Q2, Q3]), "connectionEdgeQueries" : qUnion([]), "connectionEdgeParameters" : [] }]});
        }
        {
            var Q0;
            Q0=makeQuery(id+"F0.imprint","IMPRINT",FACE,{"disambiguationData":[TD([[makeQuery(id+"F0.imprint","IMPRINT",EDGE,{"derivedFrom":sQuery(id+"F0.wireOp",EDGE,"E0")}),1.0]])]});
            var sketch = newSketch(context, id + "F4", { "sketchPlane" : qUnion([Q0])});
            skPoint(sketch, "E30", {"position": v(0, 0) * mm});
            skSolve(sketch);
        }
        {
            var Q0;
            Q0=sQuery(id+"F4.wireOp",VERTEX,"E30");
            var Q1;
            Q1=makeQuery(id+"F3.opLoft","SWEPT_BODY",BODY,{"disambiguationData":[OSD([makeQuery(id+"F0.imprint","IMPRINT",FACE,{"disambiguationData":[TD([[makeQuery(id+"F0.imprint","IMPRINT",EDGE,{"derivedFrom":sQuery(id+"F0.wireOp",EDGE,"E0")}),1.0]])]}),makeQuery(id+"F2.imprint","IMPRINT",FACE,{"disambiguationData":[TD([[makeQuery(id+"F2.imprint","IMPRINT",EDGE,{"derivedFrom":sQuery(id+"F2.wireOp",EDGE,"E15")}),1.0]])]})])]});
            hole(context, id + "F5", {"style" : HoleStyle.SIMPLE, "endStyle" : HoleEndStyle.THROUGH, "holeDiameter" : 12.7 * mm, "tappedDepth" : 12.7 * mm, "tapClearance" : 3, "locations" : qUnion([Q0]), "scope" : qUnion([Q1])});
        }
    });
